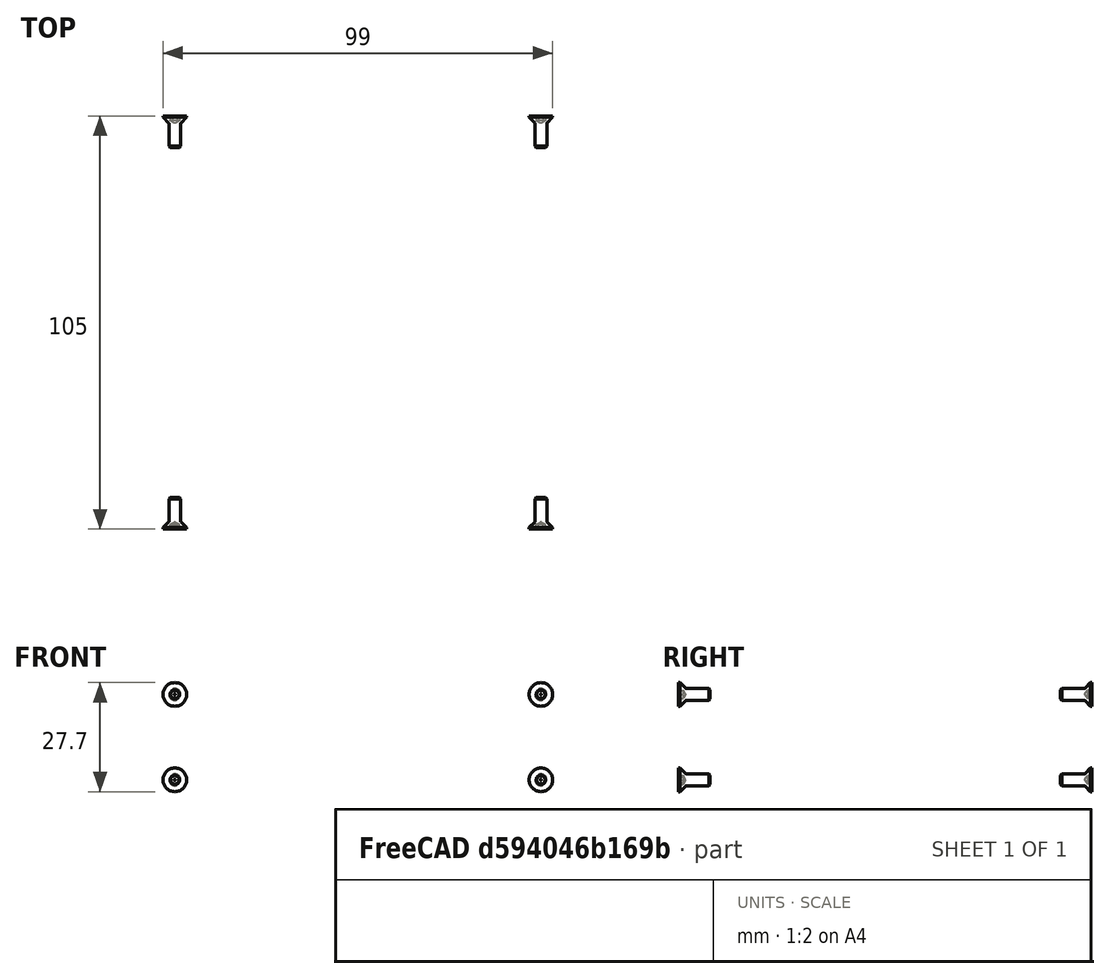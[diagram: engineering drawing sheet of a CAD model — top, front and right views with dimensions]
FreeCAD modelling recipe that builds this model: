
FCSTD DOCUMENT  (FreeCAD 0.19R24267 +99 (Git))
Label: OTP20_Case_Assembly
License: Creative Commons Attribution-NonCommercial-ShareAlike
LicenseURL: http://creativecommons.org/licenses/by-nc-sa/4.0/
objects: Part::FeaturePython×8, App::Link×6, App::DocumentObjectGroup×3, PartDesign::CoordinateSystem×1, App::FeaturePython×1, App::Part×1
note: 9 computed .brp shape members not serialized (recipe doc carries the construction recipe); baked Part::Feature solids carry a one-line shape summary decoded from their .brp
EXTERNAL_REF file=KOH_Plate_Front.FCStd obj=LCS_0
EXTERNAL_REF file=KOH_Plate_Front.FCStd obj=Plate_Front
EXTERNAL_REF file=OTP20_Case_Bezel.FCStd obj=LCS_0
EXTERNAL_REF file=OTP20_Case_Bezel.FCStd obj=Bezel
EXTERNAL_REF file=KOH-2100.FCStd obj=LCS_KOH2100_CornerBottom
EXTERNAL_REF file=KOH_Plate_Front.FCStd obj=LCS_Plate_Front_CornerBottom
EXTERNAL_REF file=KOH-2100.FCStd obj=KOH_2100
EXTERNAL_REF file=KOH-0100.FCStd obj=LCS_0
EXTERNAL_REF file=KOH-0100.FCStd obj=KOH_0100
EXTERNAL_REF file=KOH_Plate_Back.FCStd obj=LCS_Plate_Back_CornerBottom
EXTERNAL_REF file=KOH_Plate_Back.FCStd obj=Plate_Back
EXTERNAL_REF file=KOH_Plate_Back.FCStd obj=LCS_0
EXTERNAL_REF file=KOH_Plate_Front.FCStd obj=LCS_Plate_Front_DisplayCenter
EXTERNAL_REF file=../20_COTS/Waveshare_OLED_0.91in.FCStd obj=LCS_OLEDDisplay_Center
EXTERNAL_REF file=../20_COTS/Waveshare_OLED_0.91in.FCStd obj=OLED_Display

FEATURE [App::DocumentObjectGroup] Parts
FEATURE [PartDesign::CoordinateSystem] LCS_Origin  label="LCS_Case_Origin"
  AttacherType = Attacher::AttachEngine3D
  MapMode = 2
  Support = -> [X_Axis]
FEATURE [App::DocumentObjectGroup] Constraints
FEATURE [App::FeaturePython] Variables  # WARN: FeaturePython — macro-defined, semantics opaque (R4)
FEATURE [App::Link] KOH_Plate_Front_Plate_Front
  AssemblyType = Asm4EE
  AttachedBy = #LCS_0
  AttachedTo = Parent Assembly#LCS_Origin
  LinkedObject = -> <external KOH_Plate_Front.FCStd>#Plate_Front
  expr: Placement = LCS_Origin.Placement * AttachmentOffset * KOH_Plate_Front#LCS_0.Placement ^ -1
FEATURE [App::Link] OTP20_Case_Bezel_Bezel
  AssemblyType = Asm4EE
  AttachedBy = #LCS_0
  AttachedTo = Parent Assembly#LCS_Origin
  AttachmentOffset = pos=(0,2,0) rot=(0,0,1;0rad)
  LinkPlacement = pos=(0,2,0) rot=(0,0,1;0rad)
  LinkedObject = -> <external OTP20_Case_Bezel.FCStd>#Bezel
  Placement = pos=(0,2,0) rot=(0,0,1;0rad)
  expr: Placement = LCS_Origin.Placement * AttachmentOffset * OTP20_Case_Bezel#LCS_0.Placement ^ -1
FEATURE [App::Link] KOH_2100_KOH_2100
  AssemblyType = Asm4EE
  AttachedBy = #LCS_KOH2100_CornerBottom
  AttachedTo = KOH_Plate_Front_Plate_Front#LCS_Plate_Front_CornerBottom
  AttachmentOffset = pos=(0,3,0) rot=(0,0,1;0rad)
  LinkPlacement = pos=(0,3,-14.35) rot=(0,0,1;0rad)
  LinkedObject = -> <external KOH-2100.FCStd>#KOH_2100
  Placement = pos=(0,3,-14.35) rot=(0,0,1;0rad)
  expr: Placement = KOH_Plate_Front_Plate_Front.Placement * KOH_Plate_Front#LCS_Plate_Front_CornerBottom.Placement * AttachmentOffset * KOH_2100#LCS_KOH2100_CornerBottom.Placement ^ -1
FEATURE [App::Link] KOH_0100_KOH_0100
  AssemblyType = Asm4EE
  AttachedBy = #LCS_0
  AttachedTo = KOH_2100_KOH_2100#LCS_KOH2100_CornerBottom
  AttachmentOffset = pos=(105,100,28.7) rot=(0,0,1;3.14159rad)
  LinkPlacement = pos=(52.5,103,14.35) rot=(0,0,1;3.14159rad)
  LinkedObject = -> <external KOH-0100.FCStd>#KOH_0100
  Placement = pos=(52.5,103,14.35) rot=(0,0,1;3.14159rad)
  SolverId = Placement::ExpressionEngine
  expr: Placement = KOH_2100_KOH_2100.Placement * KOH_2100#LCS_KOH2100_CornerBottom.Placement * AttachmentOffset * KOH_0100#LCS_0.Placement ^ -1
FEATURE [App::Link] KOH_Plate_Back_Plate_Back
  AssemblyType = Asm4EE
  AttachedBy = #LCS_Plate_Back_CornerBottom
  AttachedTo = KOH_Plate_Front_Plate_Front#LCS_Plate_Front_CornerBottom
  AttachmentOffset = pos=(0,105,0) rot=(0,0,1;0rad)
  LinkPlacement = pos=(0,105,1.95e-14) rot=(0,0,-1;3.14159rad)
  LinkedObject = -> <external KOH_Plate_Back.FCStd>#Plate_Back
  Placement = pos=(0,105,1.95e-14) rot=(0,0,-1;3.14159rad)
  SolverId = Placement::ExpressionEngine
  expr: Placement = KOH_Plate_Front_Plate_Front.Placement * KOH_Plate_Front#LCS_Plate_Front_CornerBottom.Placement * AttachmentOffset * KOH_Plate_Back#LCS_Plate_Back_CornerBottom.Placement ^ -1
FEATURE [Part::FeaturePython] Screw  label="M3x8-Screw"  # Fasteners workbench fastener (typed FeaturePython)
  AssemblyType = Asm4EE
  AttachedBy = Origin
  AttachedTo = KOH_Plate_Front_Plate_Front#LCS_0
  AttachmentOffset = pos=(46.5,0,10.85) rot=(0,0.707107,-0.707107;3.14159rad)
  Placement = pos=(46.5,0,10.85) rot=(0,0.707107,-0.707107;3.14159rad)
  diameter = 1
  invert = false
  length = 0
  lengthCustom = 8
  matchOuter = false
  offset = 0
  thread = false
  type = 17
  expr: Placement = KOH_Plate_Front_Plate_Front.Placement * KOH_Plate_Front#LCS_0.Placement * AttachmentOffset
FEATURE [Part::FeaturePython] Screw001  label="M3x8-Screw089"  # Fasteners workbench fastener (typed FeaturePython)
  AssemblyType = Asm4EE
  AttachedBy = Origin
  AttachedTo = KOH_Plate_Front_Plate_Front#LCS_0
  AttachmentOffset = pos=(46.5,0,-10.85) rot=(1,0,0;1.5708rad)
  Placement = pos=(46.5,0,-10.85) rot=(1,0,0;1.5708rad)
  diameter = 1
  invert = false
  length = 0
  lengthCustom = 8
  matchOuter = false
  offset = 0
  thread = false
  type = 17
  expr: Placement = KOH_Plate_Front_Plate_Front.Placement * KOH_Plate_Front#LCS_0.Placement * AttachmentOffset
FEATURE [Part::FeaturePython] Screw002  label="M3x8-Screw090"  # Fasteners workbench fastener (typed FeaturePython)
  AssemblyType = Asm4EE
  AttachedBy = Origin
  AttachedTo = KOH_Plate_Front_Plate_Front#LCS_0
  AttachmentOffset = pos=(-46.5,0,10.85) rot=(-1,0,0;4.71239rad)
  Placement = pos=(-46.5,0,10.85) rot=(1,0,0;1.5708rad)
  diameter = 1
  invert = false
  length = 0
  lengthCustom = 8
  matchOuter = false
  offset = 0
  thread = false
  type = 17
  expr: Placement = KOH_Plate_Front_Plate_Front.Placement * KOH_Plate_Front#LCS_0.Placement * AttachmentOffset
FEATURE [Part::FeaturePython] Screw003  label="M3x8-Screw091"  # Fasteners workbench fastener (typed FeaturePython)
  AssemblyType = Asm4EE
  AttachedBy = Origin
  AttachedTo = KOH_Plate_Front_Plate_Front#LCS_0
  AttachmentOffset = pos=(-46.5,0,-10.85) rot=(-0.57735,-0.57735,0.57735;4.18879rad)
  Placement = pos=(-46.5,0,-10.85) rot=(0.57735,0.57735,-0.57735;2.0944rad)
  diameter = 1
  invert = false
  length = 0
  lengthCustom = 8
  matchOuter = false
  offset = 0
  thread = false
  type = 17
  expr: Placement = KOH_Plate_Front_Plate_Front.Placement * KOH_Plate_Front#LCS_0.Placement * AttachmentOffset
FEATURE [Part::FeaturePython] Screw004  label="M3x8-Screw108"  # Fasteners workbench fastener (typed FeaturePython)
  AssemblyType = Asm4EE
  AttachedBy = Origin
  AttachedTo = KOH_Plate_Back_Plate_Back#LCS_0
  AttachmentOffset = pos=(46.5,0,10.85) rot=(-1,0,0;4.71239rad)
  Placement = pos=(-46.5,105,10.85) rot=(0,0.707107,0.707107;3.14159rad)
  diameter = 1
  invert = false
  length = 0
  lengthCustom = 8
  matchOuter = false
  offset = 0
  thread = false
  type = 17
  expr: Placement = KOH_Plate_Back_Plate_Back.Placement * KOH_Plate_Back#LCS_0.Placement * AttachmentOffset
FEATURE [Part::FeaturePython] Screw005  label="M3x8-Screw109"  # Fasteners workbench fastener (typed FeaturePython)
  AssemblyType = Asm4EE
  AttachedBy = Origin
  AttachedTo = KOH_Plate_Back_Plate_Back#LCS_0
  AttachmentOffset = pos=(46.5,0,-10.85) rot=(1,0,0;1.5708rad)
  Placement = pos=(-46.5,105,-10.85) rot=(0,0.707107,0.707107;3.14159rad)
  diameter = 1
  invert = false
  length = 0
  lengthCustom = 8
  matchOuter = false
  offset = 0
  thread = false
  type = 17
  expr: Placement = KOH_Plate_Back_Plate_Back.Placement * KOH_Plate_Back#LCS_0.Placement * AttachmentOffset
FEATURE [Part::FeaturePython] Screw006  label="M3x8-Screw110"  # Fasteners workbench fastener (typed FeaturePython)
  AssemblyType = Asm4EE
  AttachedBy = Origin
  AttachedTo = KOH_Plate_Back_Plate_Back#LCS_0
  AttachmentOffset = pos=(-46.5,0,10.85) rot=(1,0,0;1.5708rad)
  Placement = pos=(46.5,105,10.85) rot=(0,0.707107,0.707107;3.14159rad)
  diameter = 1
  invert = false
  length = 0
  lengthCustom = 8
  matchOuter = false
  offset = 0
  thread = false
  type = 17
  expr: Placement = KOH_Plate_Back_Plate_Back.Placement * KOH_Plate_Back#LCS_0.Placement * AttachmentOffset
FEATURE [Part::FeaturePython] Screw007  label="M3x8-Screw111"  # Fasteners workbench fastener (typed FeaturePython)
  AssemblyType = Asm4EE
  AttachedBy = Origin
  AttachedTo = KOH_Plate_Back_Plate_Back#LCS_0
  AttachmentOffset = pos=(-46.5,0,-10.85) rot=(-1,0,0;4.71239rad)
  Placement = pos=(46.5,105,-10.85) rot=(0,0.707107,0.707107;3.14159rad)
  diameter = 1
  invert = false
  length = 0
  lengthCustom = 8
  matchOuter = false
  offset = 0
  thread = false
  type = 17
  expr: Placement = KOH_Plate_Back_Plate_Back.Placement * KOH_Plate_Back#LCS_0.Placement * AttachmentOffset
FEATURE [App::DocumentObjectGroup] Group  label="Screws"
  Group = -> [Screw,Screw001,Screw002,Screw003,Screw004,Screw005,Screw006,Screw007]
FEATURE [App::Link] Waveshare_OLED_0_91in_OLED_Display
  AssemblyType = Asm4EE
  AttachedBy = #LCS_OLEDDisplay_Center
  AttachedTo = KOH_Plate_Front_Plate_Front#LCS_Plate_Front_DisplayCenter
  AttachmentOffset = pos=(0,-0.09,-2) rot=(0,0,1;3.14159rad)
  LinkPlacement = pos=(36.19,5.3,9.55) rot=(0,-1,0;3.14159rad)
  LinkedObject = -> <external ../20_COTS/Waveshare_OLED_0.91in.FCStd>#OLED_Display
  Placement = pos=(36.19,5.3,9.55) rot=(0,-1,0;3.14159rad)
  expr: Placement = KOH_Plate_Front_Plate_Front.Placement * KOH_Plate_Front#LCS_Plate_Front_DisplayCenter.Placement * AttachmentOffset * Waveshare_OLED_0_91in#LCS_OLEDDisplay_Center.Placement ^ -1
FEATURE [App::Part] Model
  Configuration = 0
  Group = -> [LCS_Origin,Constraints,Variables,KOH_Plate_Front_Plate_Front,OTP20_Case_Bezel_Bezel,KOH_2100_KOH_2100,KOH_0100_KOH_0100,KOH_Plate_Back_Plate_Back,Group,Screw,Screw001,Screw002,Screw003,Screw004,Screw005,Screw006,Screw007,Waveshare_OLED_0_91in_OLED_Display]
  Origin = -> Origin
  Type = Assembly4 Model

RESOLVED EXTERNAL PARTS (link-assembly join: the EXTERNAL_REF files above that resolve inside this repo's crawl, each included once):
---- part ../20_COTS/Waveshare_OLED_0.91in.FCStd = doc fcstd_ae2fe7aa054e ----
FCSTD DOCUMENT  (FreeCAD 0.19R24267 +99 (Git))
Label: Waveshare_OLED_0.91in
License: Creative Commons Attribution-NonCommercial-ShareAlike
LicenseURL: http://creativecommons.org/licenses/by-nc-sa/4.0/
objects: Sketcher::SketchObject×14, PartDesign::Pad×9, PartDesign::Plane×9, PartDesign::Body×7, PartDesign::Pocket×4, PartDesign::Chamfer×4, PartDesign::Mirrored×3, PartDesign::CoordinateSystem×2, PartDesign::Boolean×1, PartDesign::Hole×1, PartDesign::LinearPattern×1, PartDesign::Fillet×1, App::Part×1
note: 75 computed .brp shape members not serialized (recipe doc carries the construction recipe); baked Part::Feature solids carry a one-line shape summary decoded from their .brp

FEATURE [Sketcher::SketchObject] Sketch
  FullyConstrained = true
  MapMode = 5
  Placement = pos=(0,0,0) rot=(1,0,0;1.5708rad)
  Support = -> [XZ_Plane]
  sketch-geometry (4):
    g0: LineSegment StartX=0 StartY=12.5 StartZ=0 EndX=36 EndY=12.5 EndZ=0
    g1: LineSegment StartX=36 StartY=12.5 StartZ=0 EndX=36 EndY=0 EndZ=0
    g2: LineSegment StartX=36 StartY=0 StartZ=0 EndX=0 EndY=0 EndZ=0
    g3: LineSegment StartX=0 StartY=0 StartZ=0 EndX=0 EndY=12.5 EndZ=0
  constraints (11):
    c: Coincident(g0,g1)
    c: Coincident(g1,g2)
    c: Coincident(g2,g3)
    c: Coincident(g3,g0)
    c: Horizontal(g0)
    c: Horizontal(g2)
    c: Vertical(g1)
    c: Vertical(g3)
    c: Distance(g3) = 12.5
    c: Distance(g0) = 36
    c: Coincident(g2,g-1)
FEATURE [PartDesign::Pad] Pad  label="Board Outline"
  Direction = (1,1,1)
  Length = 1.7
  Length2 = 100
  Placement = pos=(0,0,0) rot=(1,0,0;1.5708rad)
  Profile = -> Sketch
  Refine = true
  Type = 0
FEATURE [Sketcher::SketchObject] Sketch001
  FullyConstrained = true
  MapMode = 5
  Placement = pos=(0,0,0) rot=(1,0,0;1.5708rad)
  Support = -> [XZ_Plane]
  sketch-geometry (4):
    g0: LineSegment StartX=4 StartY=11.7 StartZ=0 EndX=34 EndY=11.7 EndZ=0
    g1: LineSegment StartX=34 StartY=11.7 StartZ=0 EndX=34 EndY=0.2 EndZ=0
    g2: LineSegment StartX=34 StartY=0.2 StartZ=0 EndX=4 EndY=0.2 EndZ=0
    g3: LineSegment StartX=4 StartY=0.2 StartZ=0 EndX=4 EndY=11.7 EndZ=0
  constraints (12):
    c: Coincident(g0,g1)
    c: Coincident(g1,g2)
    c: Coincident(g2,g3)
    c: Coincident(g3,g0)
    c: Horizontal(g0)
    c: Horizontal(g2)
    c: Vertical(g1)
    c: Vertical(g3)
    c: Distance(g0) = 30
    c: Distance(g3) = 11.5
    c: Distance(g-1,g3) = 4
    c: Distance(g-1,g2) = 0.2
FEATURE [Sketcher::SketchObject] Sketch003
  FullyConstrained = true
  MapMode = 5
  Placement = pos=(0,0,0) rot=(1,0,0;1.5708rad)
  Support = -> [XZ_Plane]
  sketch-geometry (1):
    g0: Circle CenterX=1 CenterY=2.44 CenterZ=0 NormalX=0 NormalY=0 NormalZ=1 AngleXU=0 Radius=0.5
  constraints (3):
    c: DistanceX(g-2,g0) = 1
    c: Radius(g0) = 0.5
    c: DistanceY(g-1,g0) = 2.44
FEATURE [Sketcher::SketchObject] Sketch004
  FullyConstrained = true
  MapMode = 5
  Placement = pos=(0,0,0) rot=(1,0,0;1.5708rad)
  Support = -> [XZ_Plane001]
  expr: Constraints[20] = Sketch.Constraints[9]
  expr: Constraints[19] = Sketch.Constraints[8]
  sketch-geometry (8):
    g0: LineSegment StartX=29.75 StartY=0.25 StartZ=0 EndX=35.75 EndY=0.25 EndZ=0
    g1: LineSegment StartX=35.75 StartY=0.25 StartZ=0 EndX=35.75 EndY=12.25 EndZ=0
    g2: LineSegment StartX=35.75 StartY=12.25 StartZ=0 EndX=29.75 EndY=12.25 EndZ=0
    g3: LineSegment StartX=29.75 StartY=12.25 StartZ=0 EndX=29.75 EndY=0.25 EndZ=0
    g4: LineSegment StartX=0 StartY=12.5 StartZ=0 EndX=36 EndY=12.5 EndZ=0
    g5: LineSegment StartX=36 StartY=12.5 StartZ=0 EndX=36 EndY=0 EndZ=0
    g6: LineSegment StartX=36 StartY=0 StartZ=0 EndX=0 EndY=0 EndZ=0
    g7: LineSegment StartX=0 StartY=0 StartZ=0 EndX=0 EndY=12.5 EndZ=0
  constraints (23):
    c: Coincident(g0,g1)
    c: Coincident(g1,g2)
    c: Coincident(g2,g3)
    c: Coincident(g3,g0)
    c: Horizontal(g0)
    c: Horizontal(g2)
    c: Vertical(g1)
    c: Vertical(g3)
    c: DistanceY(g0) = 0.25
    c: Distance(g1) = 12
    c: Distance(g2) = 6
    c: Coincident(g4,g5)
    c: Coincident(g5,g6)
    c: Coincident(g6,g7)
    c: Coincident(g7,g4)
    c: Horizontal(g4)
    c: Horizontal(g6)
    c: Vertical(g5)
    c: Vertical(g7)
    c: Distance(g7) = 12.5
    c: Distance(g4) = 36
    c: Coincident(g6,g-1)
    c: Distance(g0,g5) = 0.25
FEATURE [PartDesign::Pad] Pad003
  Direction = (1,1,1)
  Length = 5.5
  Length2 = 100
  Placement = pos=(0,0,0) rot=(1,0,0;1.5708rad)
  Profile = -> Sketch004
  Refine = true
  Reversed = true
  Type = 0
FEATURE [Sketcher::SketchObject] Sketch005
  FullyConstrained = true
  MapMode = 5
  Placement = pos=(35.75,0,0) rot=(0.707107,0,0.707107;3.14159rad)
  Support = -> [Pad003]
  sketch-geometry (9):
    g0: LineSegment StartX=1.85 StartY=-0.8 StartZ=0 EndX=10.65 EndY=-0.8 EndZ=0
    g1: LineSegment StartX=10.65 StartY=-0.8 StartZ=0 EndX=10.65 EndY=-4.6 EndZ=0
    g2: LineSegment StartX=10.65 StartY=-4.6 StartZ=0 EndX=8.25 EndY=-4.6 EndZ=0
    g3: LineSegment StartX=1.85 StartY=-4.6 StartZ=0 EndX=1.85 EndY=-0.8 EndZ=0
    g4: GeomPoint X=6.25 Y=-2.7 Z=0
    g5: LineSegment StartX=4.25 StartY=-4.6 StartZ=0 EndX=4.25 EndY=-5.2 EndZ=0
    g6: LineSegment StartX=4.25 StartY=-5.2 StartZ=0 EndX=8.25 EndY=-5.2 EndZ=0
    g7: LineSegment StartX=8.25 StartY=-5.2 StartZ=0 EndX=8.25 EndY=-4.6 EndZ=0
    g8: LineSegment StartX=4.25 StartY=-4.6 StartZ=0 EndX=1.85 EndY=-4.6 EndZ=0
  constraints (24):
    c: Coincident(g0,g1)
    c: Coincident(g1,g2)
    c: Coincident(g8,g3)
    c: Coincident(g3,g0)
    c: Horizontal(g0)
    c: Horizontal(g2)
    c: Vertical(g1)
    c: Vertical(g3)
    c: Symmetric(g0,g1,g4)
    c: DistanceX(g4) = 6.25
    c: Distance(g1) = 3.8
    c: Distance(g-1,g0) = 0.8
    c: Coincident(g5,g6)
    c: Horizontal(g6)
    c: Coincident(g6,g7)
    c: Vertical(g5)
    c: Coincident(g2,g7)
    c: Coincident(g8,g5)
    c: Tangent(g2,g8)
    c: Vertical(g7)
    c: Distance(g0) = 8.8
    c: Distance(g6) = 4
    c: Distance(g5) = 0.6
    c: Distance(g2) = 2.4
FEATURE [PartDesign::Pocket] Pocket
  BaseFeature = -> Pad003
  Length = 4.5
  Length2 = 100
  Placement = pos=(0,0,0) rot=(1,0,0;1.5708rad)
  Profile = -> Sketch005
  Refine = true
  Type = 0
FEATURE [Sketcher::SketchObject] Sketch006
  FullyConstrained = true
  MapMode = 5
  Placement = pos=(0,8.1e-15,12.25) rot=(0,0,1;3.14159rad)
  Support = -> [Pocket]
  sketch-geometry (8):
    g0: LineSegment StartX=-34.95 StartY=-6 StartZ=0 EndX=-34.95 EndY=-4.6 EndZ=0
    g1: LineSegment StartX=-34.95 StartY=-4.6 StartZ=0 EndX=-33.25 EndY=-4.6 EndZ=0
    g2: LineSegment StartX=-33.25 StartY=-4.6 StartZ=0 EndX=-33.25 EndY=-3.6 EndZ=0
    g3: LineSegment StartX=-33.25 StartY=-3.6 StartZ=0 EndX=-30.75 EndY=-3.6 EndZ=0
    g4: LineSegment StartX=-30.75 StartY=-3.6 StartZ=0 EndX=-30.75 EndY=-2.8 EndZ=0
    g5: LineSegment StartX=-30.75 StartY=-2.8 StartZ=0 EndX=-35.75 EndY=-2.8 EndZ=0
    g6: LineSegment StartX=-35.75 StartY=-2.8 StartZ=0 EndX=-35.75 EndY=-6 EndZ=0
    g7: LineSegment StartX=-35.75 StartY=-6 StartZ=0 EndX=-34.95 EndY=-6 EndZ=0
  constraints (24):
    c: Vertical(g0)
    c: Coincident(g0,g1)
    c: Horizontal(g1)
    c: Coincident(g1,g2)
    c: Vertical(g2)
    c: Coincident(g2,g3)
    c: Horizontal(g3)
    c: Coincident(g3,g4)
    c: Vertical(g4)
    c: Coincident(g4,g5)
    c: Horizontal(g5)
    c: Coincident(g5,g6)
    c: Vertical(g6)
    c: Coincident(g6,g7)
    c: Coincident(g7,g0)
    c: Horizontal(g7)
    c: Distance(g4) = 0.8
    c: Distance(g2) = 1
    c: DistanceY(g0) = -6
    c: DistanceX(g6) = -35.75
    c: Distance(g7) = 0.8
    c: Distance(g1,g6) = 2.5
    c: Distance(g5) = 5
    c: DistanceY(g5) = -2.8
FEATURE [PartDesign::Pocket] Pocket001
  BaseFeature = -> Pocket
  Length = 0.8
  Length2 = 100
  Placement = pos=(0,0,0) rot=(1,0,0;1.5708rad)
  Profile = -> Sketch006
  Refine = true
  Type = 0
FEATURE [PartDesign::Plane] DatumPlane  label="Symmetry Plane"
  AttachmentOffset = pos=(0,0,6.25) rot=(0,0,1;0rad)
  Length = 60
  MapMode = 5
  Placement = pos=(0,0,6.25) rot=(0,0,1;0rad)
  ResizeMode = 0
  Support = -> [XY_Plane001]
  Width = 60
FEATURE [PartDesign::Mirrored] Mirrored
  BaseFeature = -> Pocket001
  MirrorPlane = -> DatumPlane
  Originals = -> [Pocket001]
  Placement = pos=(0,0,0) rot=(1,0,0;1.5708rad)
  Refine = true
FEATURE [Sketcher::SketchObject] Sketch007
  FullyConstrained = true
  MapMode = 5
  Placement = pos=(0,5.5,-2.4e-15) rot=(-1,0,0;1.5708rad)
  Support = -> [Mirrored]
  sketch-geometry (4):
    g0: LineSegment StartX=29.75 StartY=-1.85 StartZ=0 EndX=33.95 EndY=-1.85 EndZ=0
    g1: LineSegment StartX=33.95 StartY=-1.85 StartZ=0 EndX=33.95 EndY=-2.85 EndZ=0
    g2: LineSegment StartX=33.95 StartY=-2.85 StartZ=0 EndX=29.75 EndY=-2.85 EndZ=0
    g3: LineSegment StartX=29.75 StartY=-2.85 StartZ=0 EndX=29.75 EndY=-1.85 EndZ=0
  constraints (12):
    c: Coincident(g0,g1)
    c: Coincident(g1,g2)
    c: Coincident(g2,g3)
    c: Coincident(g3,g0)
    c: Horizontal(g0)
    c: Horizontal(g2)
    c: Vertical(g1)
    c: Vertical(g3)
    c: Distance(g1) = 1
    c: Distance(g0) = 4.2
    c: DistanceX(g2) = 29.75
    c: DistanceY(g0) = -1.85
FEATURE [PartDesign::Pocket] Pocket002
  BaseFeature = -> Mirrored
  Length = 1
  Length2 = 100
  Placement = pos=(0,0,0) rot=(1,0,0;1.5708rad)
  Profile = -> Sketch007
  Refine = true
  Type = 0
FEATURE [PartDesign::Mirrored] Mirrored001
  BaseFeature = -> Pocket002
  MirrorPlane = -> DatumPlane
  Originals = -> [Pocket002]
  Placement = pos=(0,0,0) rot=(1,0,0;1.5708rad)
  Refine = true
FEATURE [Sketcher::SketchObject] Sketch008
  FullyConstrained = true
  MapMode = 5
  Placement = pos=(0,8.1e-15,12.25) rot=(0,0,1;3.14159rad)
  Support = -> [Mirrored001]
  sketch-geometry (4):
    g0: LineSegment StartX=-30 StartY=0 StartZ=0 EndX=-30 EndY=-3.3 EndZ=0
    g1: LineSegment StartX=-30 StartY=-3.3 StartZ=0 EndX=-27.8 EndY=-2.5 EndZ=0
    g2: LineSegment StartX=-27.8 StartY=-2.5 StartZ=0 EndX=-27.8 EndY=0 EndZ=0
    g3: LineSegment StartX=-27.8 StartY=0 StartZ=0 EndX=-30 EndY=0 EndZ=0
  constraints (12):
    c: PointOnObject(g0,g-1)
    c: Vertical(g0)
    c: Coincident(g0,g1)
    c: Coincident(g1,g2)
    c: PointOnObject(g2,g-1)
    c: Vertical(g2)
    c: Coincident(g2,g3)
    c: Coincident(g3,g0)
    c: DistanceX(g0) = -30
    c: Distance(g0) = 3.3
    c: Distance(g3) = 2.2
    c: Distance(g2) = 2.5
FEATURE [PartDesign::Pad] Pad004
  BaseFeature = -> Mirrored001
  Direction = (1,1,1)
  Length = 0.7
  Length2 = 100
  Placement = pos=(0,0,0) rot=(1,0,0;1.5708rad)
  Profile = -> Sketch008
  Refine = true
  Reversed = true
  Type = 0
FEATURE [PartDesign::Mirrored] Mirrored002
  BaseFeature = -> Pad004
  MirrorPlane = -> DatumPlane
  Originals = -> [Pad004]
  Placement = pos=(0,0,0) rot=(1,0,0;1.5708rad)
  Refine = true
FEATURE [PartDesign::Plane] CopyDatumPlane
  Length = 70.8999
  Placement = pos=(0,0,6.25) rot=(0,0,1;0rad)
  ResizeMode = 0
  Width = 60.9499
FEATURE [PartDesign::Plane] DatumPlane001
  AttachmentOffset = pos=(0,0,3) rot=(0,0,1;0rad)
  Length = 60
  MapMode = 5
  Placement = pos=(0,0,9.25) rot=(0,0,1;0rad)
  ResizeMode = 0
  Support = -> [CopyDatumPlane]
  Width = 60
FEATURE [Sketcher::SketchObject] Sketch009
  FullyConstrained = true
  MapMode = 5
  Placement = pos=(0,0,9.25) rot=(0,0,1;0rad)
  Support = -> [DatumPlane001]
  sketch-geometry (12):
    g0: LineSegment StartX=34.95 StartY=2.8 StartZ=0 EndX=29.95 EndY=2.8 EndZ=0
    g1: LineSegment StartX=29.65 StartY=2.5 StartZ=0 EndX=29.65 EndY=0.8 EndZ=0
    g2: LineSegment StartX=28.85 StartY=-1.6e-15 StartZ=0 EndX=27.15 EndY=0 EndZ=0
    g3: LineSegment StartX=27.15 StartY=0 StartZ=0 EndX=27.15 EndY=0.5 EndZ=0
    g4: LineSegment StartX=27.15 StartY=0.5 StartZ=0 EndX=28.85 EndY=0.5 EndZ=0
    g5: LineSegment StartX=29.15 StartY=0.8 StartZ=0 EndX=29.15 EndY=2.5 EndZ=0
    g6: LineSegment StartX=29.95 StartY=3.3 StartZ=0 EndX=34.95 EndY=3.3 EndZ=0
    g7: LineSegment StartX=34.95 StartY=3.3 StartZ=0 EndX=34.95 EndY=2.8 EndZ=0
    g8: ArcOfCircle CenterX=29.95 CenterY=2.5 CenterZ=0 NormalX=0 NormalY=0 NormalZ=1 AngleXU=0 Radius=0.3 StartAngle=1.5708 EndAngle=3.14159
    g9: ArcOfCircle CenterX=28.85 CenterY=0.8 CenterZ=0 NormalX=0 NormalY=0 NormalZ=1 AngleXU=0 Radius=0.8 StartAngle=4.71239 EndAngle=6.28319
    g10: ArcOfCircle CenterX=28.85 CenterY=0.8 CenterZ=0 NormalX=0 NormalY=0 NormalZ=1 AngleXU=0 Radius=0.3 StartAngle=4.71239 EndAngle=6.28319
    g11: ArcOfCircle CenterX=29.95 CenterY=2.5 CenterZ=0 NormalX=0 NormalY=0 NormalZ=1 AngleXU=0 Radius=0.8 StartAngle=1.5708 EndAngle=3.14159
  constraints (30):
    c: Horizontal(g0)
    c: Vertical(g1)
    c: PointOnObject(g2,g-1)
    c: Coincident(g2,g3)
    c: Vertical(g3)
    c: Coincident(g3,g4)
    c: Horizontal(g4)
    c: Vertical(g5)
    c: Horizontal(g6)
    c: Coincident(g6,g7)
    c: Coincident(g7,g0)
    c: Vertical(g7)
    c: Distance(g7) = 0.5
    c: Equal(g3,g7)
    c: DistanceY(g0) = 2.8
    c: DistanceX(g0) = 34.95
    c: Tangent(g1,g8) = -1.5708
    c: Tangent(g0,g8) = -1.5708
    c: Tangent(g2,g9) = 1.5708
    c: Tangent(g1,g9) = 1.5708
    c: Tangent(g4,g10) = -1.5708
    c: Tangent(g5,g10) = -1.5708
    c: Tangent(g5,g11) = 1.5708
    c: Tangent(g6,g11) = 1.5708
    c: Distance(g0,g1) = 5.3
    c: Distance(g1,g3) = 2.5
    c: Coincident(g10,g9)
    c: Coincident(g11,g8)
    c: Radius(g11) = 0.8
    c: Radius(g9) = 0.8
FEATURE [PartDesign::Pad] Pad005
  Direction = (1,1,1)
  Length = 0.5
  Length2 = 100
  Midplane = true
  Placement = pos=(0,0,9.25) rot=(0,0,1;0rad)
  Profile = -> Sketch009
  Refine = true
  Type = 0
FEATURE [PartDesign::Chamfer] Chamfer
  Angle = 45
  Base = -> Pad005 [Edge23,Face2]
  BaseFeature = -> Pad005
  ChamferType = 0
  FlipDirection = false
  Placement = pos=(0,0,9.25) rot=(0,0,1;0rad)
  Refine = true
  Size = 0.2
  Size2 = 1
  SupportTransform = false
FEATURE [PartDesign::Body] Body002  label="Pin001"
  Group = -> [DatumPlane001,CopyDatumPlane,Sketch009,Pad005,Chamfer]
  Origin = -> Origin002
  Tip = -> Chamfer
FEATURE [PartDesign::Plane] CopyDatumPlane001
  Length = 60
  Placement = pos=(0,0,6.25) rot=(0,0,1;0rad)
  ResizeMode = 0
  Width = 60
FEATURE [PartDesign::Plane] DatumPlane002
  AttachmentOffset = pos=(0,0,1) rot=(0,0,1;0rad)
  Length = 60
  MapMode = 5
  Placement = pos=(0,0,7.25) rot=(0,0,1;0rad)
  ResizeMode = 0
  Support = -> [CopyDatumPlane001]
  Width = 60
FEATURE [Sketcher::SketchObject] Sketch010
  FullyConstrained = true
  MapMode = 5
  Placement = pos=(0,0,7.25) rot=(0,0,1;0rad)
  Support = -> [DatumPlane002]
  sketch-geometry (12):
    g0: LineSegment StartX=34.95 StartY=2.8 StartZ=0 EndX=29.95 EndY=2.8 EndZ=0
    g1: LineSegment StartX=29.65 StartY=2.5 StartZ=0 EndX=29.65 EndY=0.8 EndZ=0
    g2: LineSegment StartX=28.85 StartY=-1.6e-15 StartZ=0 EndX=27.15 EndY=0 EndZ=0
    g3: LineSegment StartX=27.15 StartY=0 StartZ=0 EndX=27.15 EndY=0.5 EndZ=0
    g4: LineSegment StartX=27.15 StartY=0.5 StartZ=0 EndX=28.85 EndY=0.5 EndZ=0
    g5: LineSegment StartX=29.15 StartY=0.8 StartZ=0 EndX=29.15 EndY=2.5 EndZ=0
    g6: LineSegment StartX=29.95 StartY=3.3 StartZ=0 EndX=34.95 EndY=3.3 EndZ=0
    g7: LineSegment StartX=34.95 StartY=3.3 StartZ=0 EndX=34.95 EndY=2.8 EndZ=0
    g8: ArcOfCircle CenterX=29.95 CenterY=2.5 CenterZ=0 NormalX=0 NormalY=0 NormalZ=1 AngleXU=0 Radius=0.3 StartAngle=1.5708 EndAngle=3.14159
    g9: ArcOfCircle CenterX=28.85 CenterY=0.8 CenterZ=0 NormalX=0 NormalY=0 NormalZ=1 AngleXU=0 Radius=0.8 StartAngle=4.71239 EndAngle=6.28319
    g10: ArcOfCircle CenterX=28.85 CenterY=0.8 CenterZ=0 NormalX=0 NormalY=0 NormalZ=1 AngleXU=0 Radius=0.3 StartAngle=4.71239 EndAngle=6.28319
    g11: ArcOfCircle CenterX=29.95 CenterY=2.5 CenterZ=0 NormalX=0 NormalY=0 NormalZ=1 AngleXU=0 Radius=0.8 StartAngle=1.5708 EndAngle=3.14159
  constraints (30):
    c: Horizontal(g0)
    c: Vertical(g1)
    c: PointOnObject(g2,g-1)
    c: Coincident(g2,g3)
    c: Vertical(g3)
    c: Coincident(g3,g4)
    c: Horizontal(g4)
    c: Vertical(g5)
    c: Horizontal(g6)
    c: Coincident(g6,g7)
    c: Coincident(g7,g0)
    c: Vertical(g7)
    c: Distance(g7) = 0.5
    c: Equal(g3,g7)
    c: DistanceY(g0) = 2.8
    c: DistanceX(g0) = 34.95
    c: Tangent(g1,g8) = -1.5708
    c: Tangent(g0,g8) = -1.5708
    c: Tangent(g2,g9) = 1.5708
    c: Tangent(g1,g9) = 1.5708
    c: Tangent(g4,g10) = -1.5708
    c: Tangent(g5,g10) = -1.5708
    c: Tangent(g5,g11) = 1.5708
    c: Tangent(g6,g11) = 1.5708
    c: Distance(g0,g1) = 5.3
    c: Distance(g1,g3) = 2.5
    c: Coincident(g10,g9)
    c: Coincident(g11,g8)
    c: Radius(g11) = 0.8
    c: Radius(g9) = 0.8
FEATURE [PartDesign::Pad] Pad006
  Direction = (1,1,1)
  Length = 0.5
  Length2 = 100
  Midplane = true
  Placement = pos=(0,0,7.25) rot=(0,0,1;0rad)
  Profile = -> Sketch010
  Refine = true
  Type = 0
FEATURE [PartDesign::Chamfer] Chamfer001
  Angle = 45
  Base = -> Pad006 [Edge23,Face2]
  BaseFeature = -> Pad006
  ChamferType = 0
  FlipDirection = false
  Placement = pos=(0,0,7.25) rot=(0,0,1;0rad)
  Refine = true
  Size = 0.2
  Size2 = 1
  SupportTransform = false
FEATURE [PartDesign::Body] Body003  label="Pin002"
  Group = -> [DatumPlane002,CopyDatumPlane001,Sketch010,Pad006,Chamfer001]
  Origin = -> Origin003
  Tip = -> Chamfer001
FEATURE [PartDesign::Plane] CopyDatumPlane002
  Length = 60
  Placement = pos=(0,0,6.25) rot=(0,0,1;0rad)
  ResizeMode = 0
  Width = 60
FEATURE [PartDesign::Plane] DatumPlane003
  AttachmentOffset = pos=(0,0,-1) rot=(0,0,1;0rad)
  Length = 60
  MapMode = 5
  Placement = pos=(0,0,5.25) rot=(0,0,1;0rad)
  ResizeMode = 0
  Support = -> [CopyDatumPlane002]
  Width = 60
FEATURE [Sketcher::SketchObject] Sketch011
  FullyConstrained = true
  MapMode = 5
  Placement = pos=(0,0,5.25) rot=(0,0,1;0rad)
  Support = -> [DatumPlane003]
  sketch-geometry (12):
    g0: LineSegment StartX=34.95 StartY=2.8 StartZ=0 EndX=29.95 EndY=2.8 EndZ=0
    g1: LineSegment StartX=29.65 StartY=2.5 StartZ=0 EndX=29.65 EndY=0.8 EndZ=0
    g2: LineSegment StartX=28.85 StartY=-1.6e-15 StartZ=0 EndX=27.15 EndY=0 EndZ=0
    g3: LineSegment StartX=27.15 StartY=0 StartZ=0 EndX=27.15 EndY=0.5 EndZ=0
    g4: LineSegment StartX=27.15 StartY=0.5 StartZ=0 EndX=28.85 EndY=0.5 EndZ=0
    g5: LineSegment StartX=29.15 StartY=0.8 StartZ=0 EndX=29.15 EndY=2.5 EndZ=0
    g6: LineSegment StartX=29.95 StartY=3.3 StartZ=0 EndX=34.95 EndY=3.3 EndZ=0
    g7: LineSegment StartX=34.95 StartY=3.3 StartZ=0 EndX=34.95 EndY=2.8 EndZ=0
    g8: ArcOfCircle CenterX=29.95 CenterY=2.5 CenterZ=0 NormalX=0 NormalY=0 NormalZ=1 AngleXU=0 Radius=0.3 StartAngle=1.5708 EndAngle=3.14159
    g9: ArcOfCircle CenterX=28.85 CenterY=0.8 CenterZ=0 NormalX=0 NormalY=0 NormalZ=1 AngleXU=0 Radius=0.8 StartAngle=4.71239 EndAngle=6.28319
    g10: ArcOfCircle CenterX=28.85 CenterY=0.8 CenterZ=0 NormalX=0 NormalY=0 NormalZ=1 AngleXU=0 Radius=0.3 StartAngle=4.71239 EndAngle=6.28319
    g11: ArcOfCircle CenterX=29.95 CenterY=2.5 CenterZ=0 NormalX=0 NormalY=0 NormalZ=1 AngleXU=0 Radius=0.8 StartAngle=1.5708 EndAngle=3.14159
  constraints (30):
    c: Horizontal(g0)
    c: Vertical(g1)
    c: PointOnObject(g2,g-1)
    c: Coincident(g2,g3)
    c: Vertical(g3)
    c: Coincident(g3,g4)
    c: Horizontal(g4)
    c: Vertical(g5)
    c: Horizontal(g6)
    c: Coincident(g6,g7)
    c: Coincident(g7,g0)
    c: Vertical(g7)
    c: Distance(g7) = 0.5
    c: Equal(g3,g7)
    c: DistanceY(g0) = 2.8
    c: DistanceX(g0) = 34.95
    c: Tangent(g1,g8) = -1.5708
    c: Tangent(g0,g8) = -1.5708
    c: Tangent(g2,g9) = 1.5708
    c: Tangent(g1,g9) = 1.5708
    c: Tangent(g4,g10) = -1.5708
    c: Tangent(g5,g10) = -1.5708
    c: Tangent(g5,g11) = 1.5708
    c: Tangent(g6,g11) = 1.5708
    c: Distance(g0,g1) = 5.3
    c: Distance(g1,g3) = 2.5
    c: Coincident(g10,g9)
    c: Coincident(g11,g8)
    c: Radius(g11) = 0.8
    c: Radius(g9) = 0.8
FEATURE [PartDesign::Pad] Pad007
  Direction = (1,1,1)
  Length = 0.5
  Length2 = 100
  Midplane = true
  Placement = pos=(0,0,5.25) rot=(0,0,1;0rad)
  Profile = -> Sketch011
  Refine = true
  Type = 0
FEATURE [PartDesign::Chamfer] Chamfer002
  Angle = 45
  Base = -> Pad007 [Edge23,Face2]
  BaseFeature = -> Pad007
  ChamferType = 0
  FlipDirection = false
  Placement = pos=(0,0,5.25) rot=(0,0,1;0rad)
  Refine = true
  Size = 0.2
  Size2 = 1
  SupportTransform = false
FEATURE [PartDesign::Body] Body004  label="Pin003"
  Group = -> [DatumPlane003,CopyDatumPlane002,Sketch011,Pad007,Chamfer002]
  Origin = -> Origin004
  Tip = -> Chamfer002
FEATURE [PartDesign::Plane] CopyDatumPlane003
  Length = 60
  Placement = pos=(0,0,6.25) rot=(0,0,1;0rad)
  ResizeMode = 0
  Width = 60
FEATURE [PartDesign::Plane] DatumPlane004
  AttachmentOffset = pos=(0,0,-3) rot=(0,0,1;0rad)
  Length = 60
  MapMode = 5
  Placement = pos=(0,0,3.25) rot=(0,0,1;0rad)
  ResizeMode = 0
  Support = -> [CopyDatumPlane003]
  Width = 60
FEATURE [Sketcher::SketchObject] Sketch012
  FullyConstrained = true
  MapMode = 5
  Placement = pos=(0,0,3.25) rot=(0,0,1;0rad)
  Support = -> [DatumPlane004]
  sketch-geometry (12):
    g0: LineSegment StartX=34.95 StartY=2.8 StartZ=0 EndX=29.95 EndY=2.8 EndZ=0
    g1: LineSegment StartX=29.65 StartY=2.5 StartZ=0 EndX=29.65 EndY=0.8 EndZ=0
    g2: LineSegment StartX=28.85 StartY=-1.6e-15 StartZ=0 EndX=27.15 EndY=0 EndZ=0
    g3: LineSegment StartX=27.15 StartY=0 StartZ=0 EndX=27.15 EndY=0.5 EndZ=0
    g4: LineSegment StartX=27.15 StartY=0.5 StartZ=0 EndX=28.85 EndY=0.5 EndZ=0
    g5: LineSegment StartX=29.15 StartY=0.8 StartZ=0 EndX=29.15 EndY=2.5 EndZ=0
    g6: LineSegment StartX=29.95 StartY=3.3 StartZ=0 EndX=34.95 EndY=3.3 EndZ=0
    g7: LineSegment StartX=34.95 StartY=3.3 StartZ=0 EndX=34.95 EndY=2.8 EndZ=0
    g8: ArcOfCircle CenterX=29.95 CenterY=2.5 CenterZ=0 NormalX=0 NormalY=0 NormalZ=1 AngleXU=0 Radius=0.3 StartAngle=1.5708 EndAngle=3.14159
    g9: ArcOfCircle CenterX=28.85 CenterY=0.8 CenterZ=0 NormalX=0 NormalY=0 NormalZ=1 AngleXU=0 Radius=0.8 StartAngle=4.71239 EndAngle=6.28319
    g10: ArcOfCircle CenterX=28.85 CenterY=0.8 CenterZ=0 NormalX=0 NormalY=0 NormalZ=1 AngleXU=0 Radius=0.3 StartAngle=4.71239 EndAngle=6.28319
    g11: ArcOfCircle CenterX=29.95 CenterY=2.5 CenterZ=0 NormalX=0 NormalY=0 NormalZ=1 AngleXU=0 Radius=0.8 StartAngle=1.5708 EndAngle=3.14159
  constraints (30):
    c: Horizontal(g0)
    c: Vertical(g1)
    c: PointOnObject(g2,g-1)
    c: Coincident(g2,g3)
    c: Vertical(g3)
    c: Coincident(g3,g4)
    c: Horizontal(g4)
    c: Vertical(g5)
    c: Horizontal(g6)
    c: Coincident(g6,g7)
    c: Coincident(g7,g0)
    c: Vertical(g7)
    c: Distance(g7) = 0.5
    c: Equal(g3,g7)
    c: DistanceY(g0) = 2.8
    c: DistanceX(g0) = 34.95
    c: Tangent(g1,g8) = -1.5708
    c: Tangent(g0,g8) = -1.5708
    c: Tangent(g2,g9) = 1.5708
    c: Tangent(g1,g9) = 1.5708
    c: Tangent(g4,g10) = -1.5708
    c: Tangent(g5,g10) = -1.5708
    c: Tangent(g5,g11) = 1.5708
    c: Tangent(g6,g11) = 1.5708
    c: Distance(g0,g1) = 5.3
    c: Distance(g1,g3) = 2.5
    c: Coincident(g10,g9)
    c: Coincident(g11,g8)
    c: Radius(g11) = 0.8
    c: Radius(g9) = 0.8
FEATURE [PartDesign::Pad] Pad008
  Direction = (1,1,1)
  Length = 0.5
  Length2 = 100
  Midplane = true
  Placement = pos=(0,0,3.25) rot=(0,0,1;0rad)
  Profile = -> Sketch012
  Refine = true
  Type = 0
FEATURE [PartDesign::Chamfer] Chamfer003
  Angle = 45
  Base = -> Pad008 [Edge23,Face2]
  BaseFeature = -> Pad008
  ChamferType = 0
  FlipDirection = false
  Placement = pos=(0,0,3.25) rot=(0,0,1;0rad)
  Refine = true
  Size = 0.2
  Size2 = 1
  SupportTransform = false
FEATURE [PartDesign::Body] Body005  label="Pin004"
  Group = -> [DatumPlane004,CopyDatumPlane003,Sketch012,Pad008,Chamfer003]
  Origin = -> Origin005
  Tip = -> Chamfer003
FEATURE [PartDesign::Boolean] Boolean
  BaseFeature = -> Mirrored002
  Group = -> [Body002,Body003,Body004,Body005]
  Refine = true
  Type = 0
FEATURE [PartDesign::Body] Body001  label="Connector PH2.0"
  Group = -> [Sketch004,Pad003,Sketch005,Pocket,Sketch006,Pocket001,DatumPlane,Mirrored,Sketch007,Pocket002,Mirrored001,Sketch008,Pad004,Mirrored002,Boolean]
  Origin = -> Origin001
  Tip = -> Boolean
FEATURE [PartDesign::Pad] Pad001  label="Display Glas"
  BaseFeature = -> Pad
  Direction = (1,1,1)
  Length = 3.3
  Length2 = 100
  Placement = pos=(0,0,0) rot=(1,0,0;1.5708rad)
  Profile = -> Sketch001
  Refine = true
  Type = 0
FEATURE [Sketcher::SketchObject] Sketch002
  FullyConstrained = true
  MapMode = 5
  Placement = pos=(0,-3.3,1.5e-15) rot=(1,0,0;1.5708rad)
  Support = -> [Pad001]
  sketch-geometry (5):
    g0: LineSegment StartX=5.8 StartY=9.98 StartZ=0 EndX=28.18 EndY=9.98 EndZ=0
    g1: LineSegment StartX=28.18 StartY=9.98 StartZ=0 EndX=28.18 EndY=4.4 EndZ=0
    g2: LineSegment StartX=28.18 StartY=4.4 StartZ=0 EndX=5.8 EndY=4.4 EndZ=0
    g3: LineSegment StartX=5.8 StartY=4.4 StartZ=0 EndX=5.8 EndY=9.98 EndZ=0
    g4: GeomPoint X=16.99 Y=7.19 Z=0
  constraints (15):
    c: Coincident(g0,g1)
    c: Coincident(g1,g2)
    c: Coincident(g2,g3)
    c: Coincident(g3,g0)
    c: Horizontal(g0)
    c: Horizontal(g2)
    c: Vertical(g1)
    c: Vertical(g3)
    c: Distance(g0) = 22.38
    c: Distance(g3) = 5.58
    c: Distance(g-1,g3) = 5.8
    c: Distance(g-1,g2) = 4.4
    c: Symmetric(g0,g1,g4)
    c: DistanceX(g4) = 16.99
    c: DistanceY(g4) = 7.19
FEATURE [PartDesign::Pocket] Pocket003  label="Display Active Area"
  BaseFeature = -> Pad001
  Length = 0.1
  Length2 = 100
  Placement = pos=(0,0,0) rot=(1,0,0;1.5708rad)
  Profile = -> Sketch002
  Refine = true
  Type = 0
FEATURE [PartDesign::Hole] Hole
  BaseFeature = -> Pocket003
  Depth = 25
  DepthType = 0
  Diameter = 0.8
  DrillForDepth = false
  DrillPoint = 1
  DrillPointAngle = 118
  HoleCutCountersinkAngle = 90
  HoleCutCustomValues = false
  HoleCutDepth = 0
  HoleCutDiameter = 0
  HoleCutType = 0
  ModelActualThread = false
  Placement = pos=(0,0,0) rot=(1,0,0;1.5708rad)
  Profile = -> Sketch003
  Refine = true
  Reversed = true
  Tapered = false
  TaperedAngle = 90
  ThreadAngle = 0
  ThreadClass = 0
  ThreadCutOffInner = 0
  ThreadCutOffOuter = 0
  ThreadDirection = 0
  ThreadFit = 0
  ThreadPitch = 0
  ThreadSize = 0
  ThreadType = 0
  Threaded = false
FEATURE [PartDesign::LinearPattern] LinearPattern
  BaseFeature = -> Hole
  Direction = -> Z_Axis
  Length = 7.62
  Occurrences = 4
  Originals = -> [Hole]
  Placement = pos=(0,0,0) rot=(1,0,0;1.5708rad)
  Refine = true
FEATURE [PartDesign::Fillet] Fillet
  Base = -> LinearPattern [Edge2,Edge8,Edge1,Edge5]
  BaseFeature = -> LinearPattern
  Placement = pos=(0,0,0) rot=(1,0,0;1.5708rad)
  Radius = 0.5
  Refine = true
  SupportTransform = false
FEATURE [PartDesign::Body] Body  label="Mainboard"
  Group = -> [Sketch,Pad,Sketch001,Pad001,Pocket003,Sketch002,Sketch003,Hole,LinearPattern,Fillet]
  Origin = -> Origin
  Tip = -> Fillet
FEATURE [Sketcher::SketchObject] Sketch013
  FullyConstrained = true
  MapMode = 5
  Placement = pos=(0,0,0) rot=(1,0,0;1.5708rad)
  Support = -> [XZ_Plane006]
  sketch-geometry (6):
    g0: LineSegment StartX=19.5 StartY=1.7 StartZ=0 EndX=19.5 EndY=8.7 EndZ=0
    g1: LineSegment StartX=19.5 StartY=8.7 StartZ=0 EndX=6.5 EndY=8.7 EndZ=0
    g2: LineSegment StartX=6.5 StartY=8.7 StartZ=0 EndX=6.5 EndY=11.7 EndZ=0
    g3: LineSegment StartX=6.5 StartY=11.7 StartZ=0 EndX=21.5 EndY=11.7 EndZ=0
    g4: LineSegment StartX=21.5 StartY=11.7 StartZ=0 EndX=21.5 EndY=1.7 EndZ=0
    g5: LineSegment StartX=21.5 StartY=1.7 StartZ=0 EndX=19.5 EndY=1.7 EndZ=0
  constraints (18):
    c: Vertical(g0)
    c: Coincident(g0,g1)
    c: Horizontal(g1)
    c: Coincident(g1,g2)
    c: Vertical(g2)
    c: Coincident(g2,g3)
    c: Horizontal(g3)
    c: Coincident(g3,g4)
    c: Vertical(g4)
    c: Coincident(g4,g5)
    c: Coincident(g5,g0)
    c: Horizontal(g5)
    c: Distance(g5) = 2
    c: Distance(g2) = 3
    c: DistanceY(g3) = 11.7
    c: Distance(g4) = 10
    c: DistanceX(g3) = 21.5
    c: DistanceX(g2) = 6.5
FEATURE [PartDesign::Pad] Pad009
  Direction = (1,1,1)
  Length = 1.2
  Length2 = 100
  Placement = pos=(0,0,0) rot=(1,0,0;1.5708rad)
  Profile = -> Sketch013
  Refine = true
  Reversed = true
  Type = 0
FEATURE [PartDesign::Body] Body006  label="Components"
  Group = -> [Sketch013,Pad009]
  Origin = -> Origin006
  Tip = -> Pad009
FEATURE [PartDesign::CoordinateSystem] LCS_0
  AttacherType = Attacher::AttachEngine3D
  MapMode = 2
  Support = -> [X_Axis007]
FEATURE [PartDesign::CoordinateSystem] LCS_OLEDDisplay_Center
  AttacherType = Attacher::AttachEngine3D
  AttachmentOffset = pos=(16.99,7.19,3.3) rot=(0,0,1;0rad)
  MapMode = 5
  Placement = pos=(16.99,-3.3,7.19) rot=(1,0,0;1.5708rad)
  Support = -> [XZ_Plane007]
  expr: .AttachmentOffset.Base.x = Sketch002.Constraints[13]
  expr: .AttachmentOffset.Base.y = Sketch002.Constraints[14]
  expr: .AttachmentOffset.Base.z = <<Display Glas>>.Length
FEATURE [App::Part] OLED_Display
  Group = -> [LCS_0,LCS_OLEDDisplay_Center,Body,Body001,Body006]
  Origin = -> Origin007
---- part KOH-0100.FCStd = doc fcstd_208fa9221306 ----
FCSTD DOCUMENT  (FreeCAD 0.19R24267 +99 (Git))
Label: KOH-0100
License: All rights reserved
LicenseURL: http://en.wikipedia.org/wiki/All_rights_reserved
objects: Part::FeaturePython×2, Part::Feature×1, Part::Compound×1, PartDesign::CoordinateSystem×1, PartDesign::Plane×1, App::Part×1
note: 6 computed .brp shape members not serialized (recipe doc carries the construction recipe); baked Part::Feature solids carry a one-line shape summary decoded from their .brp

FEATURE [Part::Feature] Part__Feature  label="KOH 0"
  Placement = pos=(0,0,0) rot=(-1,0,0;1.5708rad)
  shape: bbox 105 x 160 x 8.533 mm, 128 faces (baked)
FEATURE [Part::Compound] Compound
  Links = -> [Part__Feature]
FEATURE [PartDesign::CoordinateSystem] LCS_0  label="LCS_KOH0100_CornerTop"
  AttacherType = Attacher::AttachEngine3D
  MapMode = 2
  Support = -> [X_Axis]
FEATURE [PartDesign::Plane] Offset
  AttachmentOffset = pos=(0,0,100) rot=(0,0,1;0rad)
  Length = 100
  MapMode = 5
  Placement = pos=(0,100,2.22e-14) rot=(0,0.707107,0.707107;3.14159rad)
  ResizeMode = 1
  Support = -> [XZ_Plane]
  Width = 100
FEATURE [Part::FeaturePython] Slice  # WARN: FeaturePython — macro-defined, semantics opaque (R4)
  Base = -> Compound
  Mode = 1
  Tolerance = 0
  Tools = -> [Offset]
FEATURE [Part::FeaturePython] Slice_child0  label="Slice.0"  # WARN: FeaturePython — macro-defined, semantics opaque (R4)
  Base = -> Slice
  FilterType = 1
  Invert = false
  OverrideMaxVal = 0
  WindowFrom = 80
  WindowTo = 100
  items = 0
FEATURE [App::Part] KOH_0100
  Group = -> [LCS_0,Part__Feature,Compound,Offset,Slice,Slice_child0]
  Origin = -> Origin
---- part KOH_Plate_Back.FCStd = doc fcstd_df4504fd72fb ----
FCSTD DOCUMENT  (FreeCAD 0.19R24267 +99 (Git))
Label: KOH_Plate_Back
License: All rights reserved
LicenseURL: http://en.wikipedia.org/wiki/All_rights_reserved
objects: Sketcher::SketchObject×2, PartDesign::CoordinateSystem×2, PartDesign::Pad×1, PartDesign::Fillet×1, PartDesign::Hole×1, PartDesign::Body×1, App::Part×1
note: 11 computed .brp shape members not serialized (recipe doc carries the construction recipe); baked Part::Feature solids carry a one-line shape summary decoded from their .brp

FEATURE [Sketcher::SketchObject] Sketch
  FullyConstrained = true
  MapMode = 5
  Placement = pos=(0,0,0) rot=(1,0,0;1.5708rad)
  Support = -> [XZ_Plane]
  sketch-geometry (4):
    g0: LineSegment StartX=-52.5 StartY=-14.35 StartZ=0 EndX=52.5 EndY=-14.35 EndZ=0
    g1: LineSegment StartX=52.5 StartY=-14.35 StartZ=0 EndX=52.5 EndY=14.35 EndZ=0
    g2: LineSegment StartX=52.5 StartY=14.35 StartZ=0 EndX=-52.5 EndY=14.35 EndZ=0
    g3: LineSegment StartX=-52.5 StartY=14.35 StartZ=0 EndX=-52.5 EndY=-14.35 EndZ=0
  constraints (10):
    c: Coincident(g0,g1)
    c: Coincident(g1,g2)
    c: Coincident(g2,g3)
    c: Coincident(g3,g0)
    c: Horizontal(g0)
    c: Vertical(g1)
    c: Symmetric(g2,g0,g-1)
    c: Symmetric(g2,g1,g-2)
    c: Distance(g2) = 105
    c: Distance(g3) = 28.7
FEATURE [PartDesign::Pad] Pad
  Direction = (1,1,1)
  Length = 2
  Length2 = 100
  Placement = pos=(0,0,0) rot=(1,0,0;1.5708rad)
  Profile = -> Sketch
  Refine = true
  Reversed = true
  Type = 0
FEATURE [PartDesign::Fillet] Fillet
  Base = -> Pad [Edge5,Edge2,Edge8,Edge1]
  BaseFeature = -> Pad
  Placement = pos=(0,0,0) rot=(1,0,0;1.5708rad)
  Radius = 2.5
  Refine = true
  SupportTransform = false
FEATURE [Sketcher::SketchObject] Sketch001
  FullyConstrained = true
  MapMode = 5
  Placement = pos=(0,0,0) rot=(1,0,0;1.5708rad)
  Support = -> [XZ_Plane]
  expr: Constraints[9] = Sketch.Constraints[9]
  expr: Constraints[8] = Sketch.Constraints[8]
  sketch-geometry (8):
    g0: LineSegment StartX=-52.5 StartY=-14.35 StartZ=0 EndX=52.5 EndY=-14.35 EndZ=0
    g1: LineSegment StartX=52.5 StartY=-14.35 StartZ=0 EndX=52.5 EndY=14.35 EndZ=0
    g2: LineSegment StartX=52.5 StartY=14.35 StartZ=0 EndX=-52.5 EndY=14.35 EndZ=0
    g3: LineSegment StartX=-52.5 StartY=14.35 StartZ=0 EndX=-52.5 EndY=-14.35 EndZ=0
    g4: Circle CenterX=46.5 CenterY=10.85 CenterZ=0 NormalX=0 NormalY=0 NormalZ=1 AngleXU=0 Radius=1.6
    g5: Circle CenterX=46.5 CenterY=-10.85 CenterZ=0 NormalX=0 NormalY=0 NormalZ=1 AngleXU=0 Radius=1.6
    g6: Circle CenterX=-46.5 CenterY=-10.85 CenterZ=0 NormalX=0 NormalY=0 NormalZ=1 AngleXU=0 Radius=1.6
    g7: Circle CenterX=-46.5 CenterY=10.85 CenterZ=0 NormalX=0 NormalY=0 NormalZ=1 AngleXU=0 Radius=1.6
  constraints (19):
    c: Coincident(g0,g1)
    c: Coincident(g1,g2)
    c: Coincident(g2,g3)
    c: Coincident(g3,g0)
    c: Horizontal(g0)
    c: Vertical(g1)
    c: Symmetric(g2,g0,g-1)
    c: Symmetric(g2,g1,g-2)
    c: Distance(g2) = 105
    c: Distance(g3) = 28.7
    c: Distance(g4,g2) = 3.5
    c: DistanceX(g-2,g4) = 46.5
    c: Diameter(g4) = 3.2
    c: Diameter(g5) = 3.2
    c: Symmetric(g5,g4,g-1)
    c: Diameter(g7) = 3.2
    c: Diameter(g6) = 3.2
    c: Symmetric(g7,g6,g-1)
    c: Symmetric(g7,g4,g-2)
FEATURE [PartDesign::Hole] Hole
  BaseFeature = -> Fillet
  Depth = 25
  DepthType = 0
  Diameter = 3.2
  DrillForDepth = false
  DrillPoint = 1
  DrillPointAngle = 118
  HoleCutCountersinkAngle = 90
  HoleCutCustomValues = false
  HoleCutDepth = 0
  HoleCutDiameter = 6.8
  HoleCutType = 2
  ModelActualThread = false
  Placement = pos=(0,0,0) rot=(1,0,0;1.5708rad)
  Profile = -> Sketch001
  Refine = true
  Tapered = false
  TaperedAngle = 90
  ThreadAngle = 0
  ThreadClass = 0
  ThreadCutOffInner = 0
  ThreadCutOffOuter = 0
  ThreadDirection = 0
  ThreadFit = 0
  ThreadPitch = 0
  ThreadSize = 0
  ThreadType = 0
  Threaded = false
FEATURE [PartDesign::Body] Body
  Group = -> [Sketch,Pad,Fillet,Sketch001,Hole]
  Origin = -> Origin
  Tip = -> Hole
FEATURE [PartDesign::CoordinateSystem] LCS_0  label="LCS_PlateBack_Center"
  AttacherType = Attacher::AttachEngine3D
  MapMode = 2
  Support = -> [X_Axis001]
FEATURE [PartDesign::CoordinateSystem] LCS_Plate_Back_CornerBottom
  AttacherType = Attacher::AttachEngine3D
  AttachmentOffset = pos=(52.5,-14.35,0) rot=(0,0.707107,0.707107;3.14159rad)
  MapMode = 5
  Placement = pos=(52.5,3.2e-15,-14.35) rot=(0,0,1;3.14159rad)
  Support = -> [XZ_Plane001]
FEATURE [App::Part] Plate_Back
  Group = -> [LCS_0,Body,LCS_Plate_Back_CornerBottom]
  Origin = -> Origin001
---- part KOH_Plate_Front.FCStd = doc fcstd_8556a17b28e3 ----
FCSTD DOCUMENT  (FreeCAD 0.19R24267 +99 (Git))
Label: KOH_Plate_Front
License: All rights reserved
LicenseURL: http://en.wikipedia.org/wiki/All_rights_reserved
objects: Sketcher::SketchObject×6, PartDesign::Hole×4, PartDesign::CoordinateSystem×3, PartDesign::Fillet×2, PartDesign::Pad×1, PartDesign::Pocket×1, PartDesign::Chamfer×1, PartDesign::Body×1, App::Part×1
note: 28 computed .brp shape members not serialized (recipe doc carries the construction recipe); baked Part::Feature solids carry a one-line shape summary decoded from their .brp

FEATURE [Sketcher::SketchObject] Sketch
  FullyConstrained = true
  MapMode = 5
  Placement = pos=(0,0,0) rot=(1,0,0;1.5708rad)
  Support = -> [XZ_Plane]
  sketch-geometry (4):
    g0: LineSegment StartX=-52.5 StartY=-14.35 StartZ=0 EndX=52.5 EndY=-14.35 EndZ=0
    g1: LineSegment StartX=52.5 StartY=-14.35 StartZ=0 EndX=52.5 EndY=14.35 EndZ=0
    g2: LineSegment StartX=52.5 StartY=14.35 StartZ=0 EndX=-52.5 EndY=14.35 EndZ=0
    g3: LineSegment StartX=-52.5 StartY=14.35 StartZ=0 EndX=-52.5 EndY=-14.35 EndZ=0
  constraints (10):
    c: Coincident(g0,g1)
    c: Coincident(g1,g2)
    c: Coincident(g2,g3)
    c: Coincident(g3,g0)
    c: Horizontal(g0)
    c: Vertical(g1)
    c: Symmetric(g2,g0,g-1)
    c: Symmetric(g2,g1,g-2)
    c: Distance(g2) = 105
    c: Distance(g3) = 28.7
FEATURE [PartDesign::Pad] Pad
  Direction = (1,1,1)
  Length = 2
  Length2 = 100
  Placement = pos=(0,0,0) rot=(1,0,0;1.5708rad)
  Profile = -> Sketch
  Refine = true
  Reversed = true
  Type = 0
FEATURE [PartDesign::Fillet] Fillet
  Base = -> Pad [Edge5,Edge2,Edge8,Edge1]
  BaseFeature = -> Pad
  Placement = pos=(0,0,0) rot=(1,0,0;1.5708rad)
  Radius = 2.5
  Refine = true
  SupportTransform = false
FEATURE [Sketcher::SketchObject] Sketch001
  FullyConstrained = true
  MapMode = 5
  Placement = pos=(0,0,0) rot=(1,0,0;1.5708rad)
  Support = -> [XZ_Plane]
  expr: Constraints[9] = Sketch.Constraints[9]
  expr: Constraints[8] = Sketch.Constraints[8]
  sketch-geometry (8):
    g0: LineSegment StartX=-52.5 StartY=-14.35 StartZ=0 EndX=52.5 EndY=-14.35 EndZ=0
    g1: LineSegment StartX=52.5 StartY=-14.35 StartZ=0 EndX=52.5 EndY=14.35 EndZ=0
    g2: LineSegment StartX=52.5 StartY=14.35 StartZ=0 EndX=-52.5 EndY=14.35 EndZ=0
    g3: LineSegment StartX=-52.5 StartY=14.35 StartZ=0 EndX=-52.5 EndY=-14.35 EndZ=0
    g4: Circle CenterX=46.5 CenterY=10.85 CenterZ=0 NormalX=0 NormalY=0 NormalZ=1 AngleXU=0 Radius=1.6
    g5: Circle CenterX=46.5 CenterY=-10.85 CenterZ=0 NormalX=0 NormalY=0 NormalZ=1 AngleXU=0 Radius=1.6
    g6: Circle CenterX=-46.5 CenterY=-10.85 CenterZ=0 NormalX=0 NormalY=0 NormalZ=1 AngleXU=0 Radius=1.6
    g7: Circle CenterX=-46.5 CenterY=10.85 CenterZ=0 NormalX=0 NormalY=0 NormalZ=1 AngleXU=0 Radius=1.6
  constraints (20):
    c: Coincident(g0,g1)
    c: Coincident(g1,g2)
    c: Coincident(g2,g3)
    c: Coincident(g3,g0)
    c: Horizontal(g0)
    c: Vertical(g1)
    c: Symmetric(g2,g0,g-1)
    c: Symmetric(g2,g1,g-2)
    c: Distance(g2) = 105
    c: Distance(g3) = 28.7
    c: Distance(g4,g2) = 3.5
    c: DistanceX(g-2,g4) = 46.5
    c: Diameter(g4) = 3.2
    c: Diameter(g5) = 3.2
    c: Symmetric(g5,g4,g-1)
    c: Diameter(g7) = 3.2
    c: Diameter(g6) = 3.2
    c: Symmetric(g7,g6,g-1)
    c: Symmetric(g7,g4,g-2)
    c: Distance(g4,g5) = 21.7
FEATURE [PartDesign::Hole] Hole
  BaseFeature = -> Fillet
  Depth = 25
  DepthType = 0
  Diameter = 3.2
  DrillForDepth = false
  DrillPoint = 1
  DrillPointAngle = 118
  HoleCutCountersinkAngle = 90
  HoleCutCustomValues = false
  HoleCutDepth = 0
  HoleCutDiameter = 6.8
  HoleCutType = 2
  ModelActualThread = false
  Placement = pos=(0,0,0) rot=(1,0,0;1.5708rad)
  Profile = -> Sketch001
  Refine = true
  Tapered = false
  TaperedAngle = 90
  ThreadAngle = 0
  ThreadClass = 0
  ThreadCutOffInner = 0
  ThreadCutOffOuter = 0
  ThreadDirection = 0
  ThreadFit = 0
  ThreadPitch = 0
  ThreadSize = 0
  ThreadType = 0
  Threaded = false
FEATURE [Sketcher::SketchObject] Sketch002  label="Cutout_FrontPanel"
  FullyConstrained = true
  MapMode = 5
  Placement = pos=(0,0,0) rot=(1,0,0;1.5708rad)
  Support = -> [XZ_Plane]
  expr: Constraints[37] = Constraints[36]
  sketch-geometry (20):
    g0: LineSegment StartX=-47.4 StartY=1.44 StartZ=0 EndX=-38.6 EndY=1.44 EndZ=0
    g1: LineSegment StartX=-38.6 StartY=1.44 StartZ=0 EndX=-38.6 EndY=-1.56 EndZ=0
    g2: LineSegment StartX=-38.6 StartY=-1.56 StartZ=0 EndX=-47.4 EndY=-1.56 EndZ=0
    g3: LineSegment StartX=-47.4 StartY=-1.56 StartZ=0 EndX=-47.4 EndY=1.44 EndZ=0
    g4: LineSegment StartX=-33 StartY=5.45 StartZ=0 EndX=-19 EndY=5.45 EndZ=0
    g5: LineSegment StartX=-19 StartY=5.45 StartZ=0 EndX=-19 EndY=-0.55 EndZ=0
    g6: LineSegment StartX=-19 StartY=-0.55 StartZ=0 EndX=-33 EndY=-0.55 EndZ=0
    g7: LineSegment StartX=-33 StartY=-0.55 StartZ=0 EndX=-33 EndY=5.45 EndZ=0
    g8: LineSegment StartX=-15 StartY=5.45 StartZ=0 EndX=-1 EndY=5.45 EndZ=0
    g9: LineSegment StartX=-1 StartY=5.45 StartZ=0 EndX=-1 EndY=-0.55 EndZ=0
    g10: LineSegment StartX=-1 StartY=-0.55 StartZ=0 EndX=-15 EndY=-0.55 EndZ=0
    g11: LineSegment StartX=-15 StartY=-0.55 StartZ=0 EndX=-15 EndY=5.45 EndZ=0
    g12: LineSegment StartX=7.45 StartY=5.7 StartZ=0 EndX=30.95 EndY=5.7 EndZ=0
    g13: LineSegment StartX=30.95 StartY=5.7 StartZ=0 EndX=30.95 EndY=-0.8 EndZ=0
    g14: LineSegment StartX=30.95 StartY=-0.8 StartZ=0 EndX=7.45 EndY=-0.8 EndZ=0
    g15: LineSegment StartX=7.45 StartY=-0.8 StartZ=0 EndX=7.45 EndY=5.7 EndZ=0
    g16: GeomPoint X=-8 Y=2.45 Z=0
    g17: GeomPoint X=-26 Y=2.45 Z=0
    g18: GeomPoint X=-43 Y=-0.06 Z=0
    g19: GeomPoint X=19.2 Y=2.45 Z=0
  constraints (55):
    c: Coincident(g0,g1)
    c: Coincident(g1,g2)
    c: Coincident(g2,g3)
    c: Coincident(g3,g0)
    c: Horizontal(g0)
    c: Horizontal(g2)
    c: Vertical(g1)
    c: Vertical(g3)
    c: Coincident(g4,g5)
    c: Coincident(g5,g6)
    c: Coincident(g6,g7)
    c: Coincident(g7,g4)
    c: Horizontal(g4)
    c: Horizontal(g6)
    c: Vertical(g5)
    c: Vertical(g7)
    c: Coincident(g8,g9)
    c: Coincident(g9,g10)
    c: Coincident(g10,g11)
    c: Coincident(g11,g8)
    c: Horizontal(g8)
    c: Horizontal(g10)
    c: Vertical(g9)
    c: Vertical(g11)
    c: Coincident(g12,g13)
    c: Coincident(g13,g14)
    c: Coincident(g14,g15)
    c: Coincident(g15,g12)
    c: Horizontal(g12)
    c: Horizontal(g14)
    c: Vertical(g13)
    c: Vertical(g15)
    c: Horizontal(g4,g8)
    c: Horizontal(g5,g10)
    c: Distance(g-1,g3) = 47.4
    c: Distance(g2) = 8.8
    c: Distance(g6) = 14
    c: Distance(g10) = 14
    c: Distance(g3) = 3
    c: Distance(g-1,g2) = 1.56
    c: Distance(g-1,g6) = 0.55
    c: Distance(g7) = 6
    c: Distance(g12) = 23.5
    c: Distance(g13) = 6.5
    c: Distance(g6,g1) = 5.6
    c: Symmetric(g8,g9,g16)
    c: Symmetric(g5,g4,g17)
    c: DistanceX(g17,g16) = 18
    c: Symmetric(g0,g1,g18)
    c: DistanceX(g18,g17) = 17
    c: Symmetric(g12,g13,g19)
    c: Horizontal(g16,g19)
    c: DistanceX(g19) = 19.2  'DisplayCenter_X'
    c: DistanceX(g8) = -15
    c: DistanceY(g19) = 2.45  'DisplayCenter_Z'
FEATURE [PartDesign::Pocket] Pocket
  BaseFeature = -> Hole
  Length = 5
  Length2 = 100
  Placement = pos=(0,0,0) rot=(1,0,0;1.5708rad)
  Profile = -> Sketch002
  Refine = true
  Type = 1
FEATURE [PartDesign::Fillet] Fillet001
  Base = -> Pocket [Edge69,Edge73,Edge83,Edge68,Edge76,Edge72,Edge82,Edge77,Edge75,Edge67,Edge71,Edge81,Edge84,Edge74,Edge70,Edge78]
  BaseFeature = -> Pocket
  Placement = pos=(0,0,0) rot=(1,0,0;1.5708rad)
  Radius = 0.75
  Refine = true
  SupportTransform = false
FEATURE [PartDesign::Chamfer] Chamfer
  Angle = 45
  Base = -> Fillet001 [Edge40,Edge24,Edge4,Edge32]
  BaseFeature = -> Fillet001
  ChamferType = 0
  FlipDirection = false
  Placement = pos=(0,0,0) rot=(1,0,0;1.5708rad)
  Refine = true
  Size = 0.5
  Size2 = 1
  SupportTransform = false
FEATURE [Sketcher::SketchObject] Sketch003
  FullyConstrained = true
  MapMode = 5
  Placement = pos=(0,0,0) rot=(1,0,0;1.5708rad)
  Support = -> [XZ_Plane]
  sketch-geometry (3):
    g0: Circle CenterX=38 CenterY=0.94 CenterZ=0 NormalX=0 NormalY=0 NormalZ=1 AngleXU=0 Radius=0.5
    g1: Circle CenterX=38 CenterY=3.48 CenterZ=0 NormalX=0 NormalY=0 NormalZ=1 AngleXU=0 Radius=0.5
    g2: LineSegment StartX=38 StartY=0.94 StartZ=0 EndX=38 EndY=3.48 EndZ=0
  constraints (8):
    c: Diameter(g0) = 1
    c: DistanceX(g-2,g0) = 38
    c: Diameter(g1) = 1
    c: Coincident(g0,g2)
    c: Coincident(g1,g2)
    c: Distance(g2) = 2.54
    c: Angle(g2) = 1.5708
    c: DistanceY(g-1,g0) = 0.94
FEATURE [PartDesign::Hole] Hole001
  BaseFeature = -> Chamfer
  Depth = 25
  DepthType = 0
  Diameter = 1.95
  DrillForDepth = false
  DrillPoint = 1
  DrillPointAngle = 118
  HoleCutCountersinkAngle = 90
  HoleCutCustomValues = false
  HoleCutDepth = 0
  HoleCutDiameter = 6.1
  HoleCutType = 0
  ModelActualThread = false
  Placement = pos=(0,0,0) rot=(1,0,0;1.5708rad)
  Profile = -> Sketch003
  Refine = true
  Tapered = false
  TaperedAngle = 90
  ThreadAngle = 0
  ThreadClass = 0
  ThreadCutOffInner = 0
  ThreadCutOffOuter = 0
  ThreadDirection = 0
  ThreadFit = 0
  ThreadPitch = 0
  ThreadSize = 0
  ThreadType = 0
  Threaded = false
FEATURE [Sketcher::SketchObject] Sketch004
  FullyConstrained = true
  MapMode = 5
  Placement = pos=(0,0,0) rot=(1,0,0;1.5708rad)
  Support = -> [XZ_Plane]
  sketch-geometry (1):
    g0: Circle CenterX=46.5 CenterY=0 CenterZ=0 NormalX=0 NormalY=0 NormalZ=1 AngleXU=0 Radius=2.5
  constraints (3):
    c: PointOnObject(g0,g-1)
    c: DistanceX(g-2,g0) = 46.5
    c: Diameter(g0) = 5
FEATURE [PartDesign::CoordinateSystem] LCS_0  label="LCS_PlateFront_Center"
  AttacherType = Attacher::AttachEngine3D
  MapMode = 2
  Support = -> [X_Axis001]
FEATURE [PartDesign::Hole] Hole002
  BaseFeature = -> Hole001
  Depth = 25
  DepthType = 0
  Diameter = 6
  DrillForDepth = false
  DrillPoint = 1
  DrillPointAngle = 118
  HoleCutCountersinkAngle = 90
  HoleCutCustomValues = false
  HoleCutDepth = 0
  HoleCutDiameter = 6.1
  HoleCutType = 0
  ModelActualThread = false
  Placement = pos=(0,0,0) rot=(1,0,0;1.5708rad)
  Profile = -> Sketch004
  Refine = true
  Tapered = false
  TaperedAngle = 90
  ThreadAngle = 0
  ThreadClass = 0
  ThreadCutOffInner = 0
  ThreadCutOffOuter = 0
  ThreadDirection = 0
  ThreadFit = 0
  ThreadPitch = 0
  ThreadSize = 0
  ThreadType = 0
  Threaded = false
FEATURE [Sketcher::SketchObject] Sketch005
  FullyConstrained = false
  MapMode = 5
  Placement = pos=(0,0,0) rot=(1,0,0;1.5708rad)
  Support = -> [XZ_Plane]
  sketch-geometry (8):
    g0: LineSegment StartX=4.18177 StartY=10.0524 StartZ=0 EndX=34.1388 EndY=10.0524 EndZ=0
    g1: LineSegment StartX=34.1388 StartY=10.0524 StartZ=0 EndX=34.1388 EndY=-3.89591 EndZ=0
    g2: LineSegment StartX=34.1388 StartY=-3.89591 StartZ=0 EndX=4.18177 EndY=-3.89591 EndZ=0
    g3: LineSegment StartX=4.18177 StartY=-3.89591 StartZ=0 EndX=4.18177 EndY=10.0524 EndZ=0
    g4: Circle CenterX=4.18177 CenterY=10.0524 CenterZ=0 NormalX=0 NormalY=0 NormalZ=1 AngleXU=0 Radius=1.30359
    g5: Circle CenterX=34.1388 CenterY=10.0524 CenterZ=0 NormalX=0 NormalY=0 NormalZ=1 AngleXU=0 Radius=1.36838
    g6: Circle CenterX=34.1388 CenterY=-3.89591 CenterZ=0 NormalX=0 NormalY=0 NormalZ=1 AngleXU=0 Radius=1.83105
    g7: Circle CenterX=4.18177 CenterY=-3.89591 CenterZ=0 NormalX=0 NormalY=0 NormalZ=1 AngleXU=0 Radius=1.53393
  constraints (12):
    c: Coincident(g0,g1)
    c: Coincident(g1,g2)
    c: Coincident(g2,g3)
    c: Coincident(g3,g0)
    c: Horizontal(g0)
    c: Horizontal(g2)
    c: Vertical(g1)
    c: Vertical(g3)
    c: Coincident(g4,g0)
    c: Coincident(g5,g0)
    c: Coincident(g6,g1)
    c: Coincident(g7,g2)
FEATURE [PartDesign::Hole] Hole003
  BaseFeature = -> Hole002
  Depth = 25
  DepthType = 0
  Diameter = 1.6
  DrillForDepth = false
  DrillPoint = 1
  DrillPointAngle = 118
  HoleCutCountersinkAngle = 90
  HoleCutCustomValues = false
  HoleCutDepth = 0
  HoleCutDiameter = 3
  HoleCutType = 2
  ModelActualThread = false
  Placement = pos=(0,0,0) rot=(1,0,0;1.5708rad)
  Profile = -> Sketch005
  Refine = true
  Tapered = false
  TaperedAngle = 90
  ThreadAngle = 0
  ThreadClass = 0
  ThreadCutOffInner = 0
  ThreadCutOffOuter = 0
  ThreadDirection = 0
  ThreadFit = 0
  ThreadPitch = 0
  ThreadSize = 0
  ThreadType = 0
  Threaded = false
FEATURE [PartDesign::Body] Body
  Group = -> [Sketch,Pad,Fillet,Sketch001,Hole,Sketch002,Pocket,Fillet001,Chamfer,Sketch003,Hole001,Sketch004,Hole002,Sketch005,Hole003]
  Origin = -> Origin
  Tip = -> Hole002
FEATURE [PartDesign::CoordinateSystem] LCS_Plate_Front_CornerBottom
  AttacherType = Attacher::AttachEngine3D
  AttachmentOffset = pos=(-52.5,-14.35,0) rot=(-1,0,0;1.5708rad)
  MapMode = 5
  Placement = pos=(-52.5,3.2e-15,-14.35) rot=(0,0,1;0rad)
  Support = -> [XZ_Plane001]
FEATURE [PartDesign::CoordinateSystem] LCS_Plate_Front_DisplayCenter
  AttacherType = Attacher::AttachEngine3D
  AttachmentOffset = pos=(19.2,2.45,0) rot=(0,0,1;0rad)
  MapMode = 5
  Placement = pos=(19.2,-5e-16,2.45) rot=(1,0,0;1.5708rad)
  Support = -> [XZ_Plane001]
  expr: .AttachmentOffset.Base.x = Sketch002.Constraints.DisplayCenter_X
  expr: .AttachmentOffset.Base.y = Sketch002.Constraints.DisplayCenter_Z
FEATURE [App::Part] Plate_Front
  Group = -> [LCS_0,Body,LCS_Plate_Front_CornerBottom,LCS_Plate_Front_DisplayCenter]
  Origin = -> Origin001
---- part OTP20_Case_Bezel.FCStd = doc fcstd_8eea7158c41d ----
FCSTD DOCUMENT  (FreeCAD 0.19R24267 +99 (Git))
Label: OTP20_Case_Bezel
License: All rights reserved
LicenseURL: http://en.wikipedia.org/wiki/All_rights_reserved
objects: Sketcher::SketchObject×15, PartDesign::Pad×13, PartDesign::Body×5, PartDesign::Fillet×5, PartDesign::Plane×4, PartDesign::LinearPattern×4, PartDesign::Mirrored×3, PartDesign::MultiTransform×3, PartDesign::Thickness×2, PartDesign::Pocket×2, PartDesign::Hole×2, PartDesign::CoordinateSystem×1, PartDesign::Boolean×1, PartDesign::Chamfer×1, App::Part×1
note: 86 computed .brp shape members not serialized (recipe doc carries the construction recipe); baked Part::Feature solids carry a one-line shape summary decoded from their .brp

FEATURE [PartDesign::Plane] DatumPlane
  AttachmentOffset = pos=(0,0,2.5) rot=(0,0,1;0rad)
  Length = 60
  MapMode = 2
  Placement = pos=(0,-2.5,-6e-16) rot=(1,0,0;1.5708rad)
  ResizeMode = 0
  Support = -> [XZ_Plane001]
  Width = 60
  expr: .AttachmentOffset.Base.z = Pad002.Length
FEATURE [Sketcher::SketchObject] Sketch  label="Sketch001"
  FullyConstrained = true
  MapMode = 5
  Placement = pos=(0,-2.5,-6e-16) rot=(1,0,0;1.5708rad)
  Support = -> [DatumPlane]
  sketch-geometry (6):
    g0: LineSegment StartX=55 StartY=6.95 StartZ=0 EndX=55 EndY=10.45 EndZ=0
    g1: LineSegment StartX=55 StartY=10.45 StartZ=0 EndX=54.2 EndY=10.45 EndZ=0
    g2: ArcOfCircle CenterX=54.2 CenterY=10.25 CenterZ=0 NormalX=0 NormalY=0 NormalZ=1 AngleXU=0 Radius=0.2 StartAngle=1.5708 EndAngle=3.14159
    g3: LineSegment StartX=54 StartY=10.25 StartZ=0 EndX=54 EndY=7.15 EndZ=0
    g4: ArcOfCircle CenterX=54.2 CenterY=7.15 CenterZ=0 NormalX=0 NormalY=0 NormalZ=1 AngleXU=0 Radius=0.2 StartAngle=3.14159 EndAngle=4.71239
    g5: LineSegment StartX=54.2 StartY=6.95 StartZ=0 EndX=55 EndY=6.95 EndZ=0
  constraints (16):
    c: Vertical(g0)
    c: Coincident(g0,g1)
    c: Horizontal(g1)
    c: Tangent(g1,g2) = -1.5708
    c: Tangent(g3,g4) = -1.5708
    c: Coincident(g5,g0)
    c: Vertical(g3)
    c: Tangent(g4,g5) = -1.5708
    c: Tangent(g2,g3) = -1.5708
    c: Horizontal(g5)
    c: Vertical(g2,g4)
    c: Radius(g4) = 0.2
    c: Distance(g0,g3) = 1
    c: Distance(g0) = 3.5
    c: Distance(g-1,g5) = 6.95
    c: Distance(g-1,g3) = 54
FEATURE [PartDesign::LinearPattern] LinearPattern
  Direction = -> Sketch [V_Axis]
  Length = 17.4
  Occurrences = 4
  Refine = true
  Reversed = true
FEATURE [PartDesign::Mirrored] Mirrored
  MirrorPlane = -> Sketch [V_Axis]
  Refine = true
FEATURE [Sketcher::SketchObject] Sketch001  label="Sketch002"
  FullyConstrained = true
  MapMode = 5
  Placement = pos=(0,-2.5,-6e-16) rot=(1,0,0;1.5708rad)
  Support = -> [DatumPlane]
  sketch-geometry (6):
    g0: LineSegment StartX=44.65 StartY=16.85 StartZ=0 EndX=44.65 EndY=16.05 EndZ=0
    g1: ArcOfCircle CenterX=44.85 CenterY=16.05 CenterZ=0 NormalX=0 NormalY=0 NormalZ=1 AngleXU=0 Radius=0.2 StartAngle=3.14159 EndAngle=4.71239
    g2: LineSegment StartX=44.85 StartY=15.85 StartZ=0 EndX=47.95 EndY=15.85 EndZ=0
    g3: ArcOfCircle CenterX=47.95 CenterY=16.05 CenterZ=0 NormalX=0 NormalY=0 NormalZ=1 AngleXU=0 Radius=0.2 StartAngle=4.71239 EndAngle=6.28319
    g4: LineSegment StartX=48.15 StartY=16.05 StartZ=0 EndX=48.15 EndY=16.85 EndZ=0
    g5: LineSegment StartX=48.15 StartY=16.85 StartZ=0 EndX=44.65 EndY=16.85 EndZ=0
  constraints (16):
    c: Vertical(g0)
    c: Tangent(g0,g1) = -1.5708
    c: Tangent(g1,g2) = -1.5708
    c: Tangent(g2,g3) = -1.5708
    c: Tangent(g3,g4) = -1.5708
    c: Coincident(g4,g5)
    c: Coincident(g5,g0)
    c: Horizontal(g5)
    c: Horizontal(g2)
    c: Vertical(g4)
    c: Horizontal(g1,g3)
    c: Radius(g3) = 0.2
    c: Distance(g0,g2) = 1
    c: Distance(g5) = 3.5
    c: Distance(g-1,g2) = 15.85
    c: Distance(g-1,g0) = 44.65
FEATURE [PartDesign::LinearPattern] LinearPattern001
  Direction = -> Sketch001 [H_Axis]
  Length = 92.8
  Occurrences = 17
  Refine = true
  Reversed = true
FEATURE [PartDesign::Mirrored] Mirrored001
  MirrorPlane = -> Sketch001 [H_Axis]
  Refine = true
FEATURE [PartDesign::CoordinateSystem] LCS_0  label="LCS_Bezel_Center"
  AttacherType = Attacher::AttachEngine3D
  MapMode = 2
  Support = -> [X_Axis002]
FEATURE [Sketcher::SketchObject] Sketch004  label="Sketch005"
  FullyConstrained = true
  MapMode = 5
  Placement = pos=(0,0,0) rot=(1,0,0;1.5708rad)
  Support = -> [XZ_Plane003]
  sketch-geometry (1):
    g0: Circle CenterX=46.5 CenterY=0 CenterZ=0 NormalX=0 NormalY=0 NormalZ=1 AngleXU=0 Radius=2.9
  constraints (3):
    c: PointOnObject(g0,g-1)
    c: Radius(g0) = 2.9
    c: DistanceX(g0) = 46.5
FEATURE [Sketcher::SketchObject] Sketch005  label="Sketch006"
  FullyConstrained = true
  MapMode = 5
  Placement = pos=(0,0,0) rot=(1,0,0;1.5708rad)
  Support = -> [XZ_Plane003]
  sketch-geometry (5):
    g0: LineSegment StartX=41.5 StartY=1 StartZ=0 EndX=50.5 EndY=1 EndZ=0
    g1: LineSegment StartX=50.5 StartY=1 StartZ=0 EndX=50.5 EndY=-1 EndZ=0
    g2: LineSegment StartX=50.5 StartY=-1 StartZ=0 EndX=41.5 EndY=-1 EndZ=0
    g3: LineSegment StartX=41.5 StartY=-1 StartZ=0 EndX=41.5 EndY=1 EndZ=0
    g4: GeomPoint X=46 Y=0 Z=0
  constraints (13):
    c: Coincident(g0,g1)
    c: Coincident(g1,g2)
    c: Coincident(g2,g3)
    c: Coincident(g3,g0)
    c: Horizontal(g0)
    c: Horizontal(g2)
    c: Vertical(g1)
    c: Vertical(g3)
    c: PointOnObject(g4,g-1)
    c: Symmetric(g0,g1,g4)
    c: Distance(g1) = 2
    c: DistanceX(g0) = 50.5
    c: Distance(g2) = 9
FEATURE [PartDesign::Pad] Pad004
  Direction = (1,1,1)
  Length = 1
  Length2 = 100
  Placement = pos=(0,0,0) rot=(1,0,0;1.5708rad)
  Profile = -> Sketch005
  Refine = true
  Reversed = true
  Type = 0
FEATURE [PartDesign::Pad] Pad005
  BaseFeature = -> Pad004
  Direction = (1,1,1)
  Length = 1
  Length2 = 100
  Placement = pos=(0,0,0) rot=(1,0,0;1.5708rad)
  Profile = -> Sketch004
  Refine = true
  Reversed = true
  Type = 0
FEATURE [PartDesign::Plane] DatumPlane001  label="Display Start"
  AttachmentOffset = pos=(0,0,0.2) rot=(0,0,1;0rad)
  Length = 60
  MapMode = 5
  Placement = pos=(0.2,0,0) rot=(0.57735,0.57735,0.57735;2.0944rad)
  ResizeMode = 0
  Support = -> [YZ_Plane004]
  Width = 60
FEATURE [Sketcher::SketchObject] Sketch006  label="Sketch007"
  FullyConstrained = true
  MapMode = 5
  Placement = pos=(0.2,0,0) rot=(0.57735,0.57735,0.57735;2.0944rad)
  Support = -> [DatumPlane001]
  sketch-geometry (7):
    g0: LineSegment StartX=1 StartY=14.35 StartZ=0 EndX=1 EndY=10.35 EndZ=0
    g1: ArcOfCircle CenterX=4.1 CenterY=9.55 CenterZ=0 NormalX=0 NormalY=0 NormalZ=1 AngleXU=0 Radius=0.8 StartAngle=3.14159 EndAngle=6.28319
    g2: LineSegment StartX=3.3 StartY=9.55 StartZ=0 EndX=0 EndY=9.55 EndZ=0
    g3: LineSegment StartX=0 StartY=9.55 StartZ=0 EndX=0 EndY=14.35 EndZ=0
    g4: LineSegment StartX=0 StartY=14.35 StartZ=0 EndX=1 EndY=14.35 EndZ=0
    g5: LineSegment StartX=1 StartY=10.35 StartZ=0 EndX=4.9 EndY=10.35 EndZ=0
    g6: LineSegment StartX=4.9 StartY=10.35 StartZ=0 EndX=4.9 EndY=9.55 EndZ=0
  constraints (22):
    c: Vertical(g0)
    c: Coincident(g2,g3)
    c: Coincident(g3,g4)
    c: Coincident(g4,g0)
    c: Distance(g4) = 1
    c: Horizontal(g4)
    c: Radius(g1) = 0.8
    c: DistanceY(g0) = 14.35
    c: Horizontal(g1,g1)
    c: Horizontal(g1,g1)
    c: Vertical(g3)
    c: Horizontal(g2)
    c: Coincident(g0,g5)
    c: Horizontal(g5)
    c: Coincident(g5,g6)
    c: Coincident(g6,g1)
    c: Vertical(g6)
    c: Distance(g6) = 0.8
    c: Coincident(g2,g1)
    c: DistanceX(g1) = 3.3
    c: PointOnObject(g2,g-2)
    c: DistanceY(g1) = 9.55
FEATURE [Sketcher::SketchObject] Sketch007  label="Sketch008"
  FullyConstrained = true
  MapMode = 5
  Placement = pos=(0.2,0,0) rot=(0.57735,0.57735,0.57735;2.0944rad)
  Support = -> [DatumPlane001]
  sketch-geometry (7):
    g0: LineSegment StartX=1 StartY=-14.35 StartZ=0 EndX=1 EndY=-4.56714 EndZ=0
    g1: LineSegment StartX=1 StartY=-4.56714 StartZ=0 EndX=4.5 EndY=-3.95 EndZ=0
    g2: LineSegment StartX=4.5 StartY=-3.95 StartZ=0 EndX=4.5 EndY=-2.95 EndZ=0
    g3: ArcOfCircle CenterX=3.9 CenterY=-2.95 CenterZ=0 NormalX=0 NormalY=0 NormalZ=1 AngleXU=0 Radius=0.6 StartAngle=0 EndAngle=3.14159
    g4: LineSegment StartX=3.3 StartY=-2.95 StartZ=0 EndX=0 EndY=-3.53188 EndZ=0
    g5: LineSegment StartX=0 StartY=-3.53188 StartZ=0 EndX=0 EndY=-14.35 EndZ=0
    g6: LineSegment StartX=0 StartY=-14.35 StartZ=0 EndX=1 EndY=-14.35 EndZ=0
  constraints (21):
    c: Vertical(g0)
    c: Coincident(g0,g1)
    c: Coincident(g1,g2)
    c: Tangent(g2,g3) = -1.5708
    c: Coincident(g3,g4)
    c: PointOnObject(g4,g-2)
    c: Coincident(g4,g5)
    c: PointOnObject(g5,g-2)
    c: Coincident(g5,g6)
    c: Coincident(g6,g0)
    c: Horizontal(g6)
    c: Distance(g6) = 1
    c: Radius(g3) = 0.6
    c: Vertical(g2)
    c: Distance(g2) = 1
    c: DistanceX(g3) = 3.3
    c: DistanceY(g3) = -2.95
    c: DistanceY(g5) = -14.35
    c: Horizontal(g3,g3)
    c: Parallel(g4,g1)
    c: Angle(g-1,g4) = 0.174533
FEATURE [Sketcher::SketchObject] Sketch008  label="Sketch009"
  FullyConstrained = true
  MapMode = 5
  Placement = pos=(0.2,0,0) rot=(0.57735,0.57735,0.57735;2.0944rad)
  Support = -> [DatumPlane001]
  expr: Constraints[19] = Sketch006.Constraints[19] + Sketch006.Constraints[6]
  expr: Constraints[14] = Sketch006.Constraints[17]
  expr: Constraints[5] = Sketch006.Constraints[6]
  expr: Constraints[6] = Sketch006.Constraints[7]
  expr: Constraints[3] = Sketch006.Constraints[4]
  expr: Constraints[20] = Sketch006.Constraints[21]
  sketch-geometry (7):
    g0: LineSegment StartX=1 StartY=14.35 StartZ=0 EndX=1 EndY=10.35 EndZ=0
    g1: ArcOfCircle CenterX=4.1 CenterY=9.55 CenterZ=0 NormalX=0 NormalY=0 NormalZ=1 AngleXU=0 Radius=0.8 StartAngle=4.71239 EndAngle=6.28319
    g2: LineSegment StartX=0 StartY=8.75 StartZ=0 EndX=0 EndY=14.35 EndZ=0
    g3: LineSegment StartX=0 StartY=14.35 StartZ=0 EndX=1 EndY=14.35 EndZ=0
    g4: LineSegment StartX=1 StartY=10.35 StartZ=0 EndX=4.9 EndY=10.35 EndZ=0
    g5: LineSegment StartX=4.9 StartY=10.35 StartZ=0 EndX=4.9 EndY=9.55 EndZ=0
    g6: LineSegment StartX=0 StartY=8.75 StartZ=0 EndX=4.1 EndY=8.75 EndZ=0
  constraints (21):
    c: Vertical(g0)
    c: Coincident(g2,g3)
    c: Coincident(g3,g0)
    c: Distance(g3) = 1
    c: Horizontal(g3)
    c: Radius(g1) = 0.8
    c: DistanceY(g0) = 14.35
    c: Horizontal(g1,g1)
    c: Vertical(g2)
    c: Coincident(g0,g4)
    c: Horizontal(g4)
    c: Coincident(g4,g5)
    c: Coincident(g5,g1)
    c: Vertical(g5)
    c: Distance(g5) = 0.8
    c: PointOnObject(g2,g-2)
    c: Coincident(g6,g2)
    c: Horizontal(g6)
    c: Tangent(g1,g6) = -1.5708
    c: DistanceX(g1) = 4.1
    c: DistanceY(g1) = 9.55
FEATURE [PartDesign::Plane] DatumPlane002  label="Display End"
  AttachmentOffset = pos=(0,0,36) rot=(0,0,1;0rad)
  Length = 60
  MapMode = 5
  Placement = pos=(36.2,-4e-15,4e-15) rot=(0.57735,0.57735,0.57735;2.0944rad)
  ResizeMode = 0
  Support = -> [DatumPlane001]
  Width = 60
FEATURE [PartDesign::Pad] Pad006
  Direction = (1,1,1)
  Length = 36
  Length2 = 36
  Placement = pos=(0.2,0,0) rot=(0.57735,0.57735,0.57735;2.0944rad)
  Profile = -> Sketch006
  Refine = true
  Type = 3
  UpToFace = -> DatumPlane002 [Plane]
FEATURE [PartDesign::Pad] Pad007
  Direction = (1,1,1)
  Length = 36
  Length2 = 100
  Placement = pos=(0.2,0,0) rot=(0.57735,0.57735,0.57735;2.0944rad)
  Profile = -> Sketch007
  Refine = true
  Type = 3
  UpToFace = -> DatumPlane002 [Plane]
FEATURE [PartDesign::Pad] Pad008
  BaseFeature = -> Pad006
  Direction = (1,1,1)
  Length = 1
  Length2 = 100
  Placement = pos=(0.2,0,0) rot=(0.57735,0.57735,0.57735;2.0944rad)
  Profile = -> Sketch008
  Refine = true
  Reversed = true
  Type = 0
FEATURE [PartDesign::Plane] DatumPlane003  label="Display Symmetry"
  AttachmentOffset = pos=(0,0,18) rot=(0,0,1;0rad)
  Length = 60
  MapMode = 5
  Placement = pos=(18.2,-2e-15,2e-15) rot=(0.57735,0.57735,0.57735;2.0944rad)
  ResizeMode = 0
  Support = -> [DatumPlane001]
  Width = 60
  expr: .AttachmentOffset.Base.z = <<Display End>>.AttachmentOffset.Base[2] * 0.5
FEATURE [PartDesign::Mirrored] Mirrored002
  BaseFeature = -> Pad008
  MirrorPlane = -> DatumPlane003
  Originals = -> [Pad008]
  Placement = pos=(0.2,0,0) rot=(0.57735,0.57735,0.57735;2.0944rad)
  Refine = true
FEATURE [PartDesign::Body] Body003  label="Display Frame Top"
  Group = -> [Sketch006,Pad006,Sketch008,Pad008,DatumPlane001,DatumPlane002,DatumPlane003,Mirrored002]
  Origin = -> Origin004
  Tip = -> Mirrored002
FEATURE [Sketcher::SketchObject] Sketch009  label="Sketch010"
  FullyConstrained = true
  MapMode = 5
  Placement = pos=(0.2,0,0) rot=(0.57735,0.57735,0.57735;2.0944rad)
  Support = -> [DatumPlane001]
  expr: Constraints[4] = Sketch007.Constraints[14]
  expr: Constraints[2] = Sketch007.Constraints[12]
  expr: Constraints[5] = Sketch007.Constraints[11]
  expr: Constraints[6] = Sketch007.Constraints[20]
  expr: Constraints[11] = Sketch007.Constraints[15] + Sketch007.Constraints[12]
  expr: Constraints[13] = Sketch007.Constraints[16]
  expr: Constraints[19] = Sketch007.Constraints[17]
  sketch-geometry (7):
    g0: LineSegment StartX=1 StartY=-4.56714 StartZ=0 EndX=4.5 EndY=-3.95 EndZ=0
    g1: LineSegment StartX=4.5 StartY=-3.95 StartZ=0 EndX=4.5 EndY=-2.95 EndZ=0
    g2: ArcOfCircle CenterX=3.9 CenterY=-2.95 CenterZ=0 NormalX=0 NormalY=0 NormalZ=1 AngleXU=0 Radius=0.6 StartAngle=0 EndAngle=1.5708
    g3: LineSegment StartX=3.9 StartY=-2.35 StartZ=0 EndX=0 EndY=-2.35 EndZ=0
    g4: LineSegment StartX=0 StartY=-2.35 StartZ=0 EndX=0 EndY=-14.35 EndZ=0
    g5: LineSegment StartX=0 StartY=-14.35 StartZ=0 EndX=1 EndY=-14.35 EndZ=0
    g6: LineSegment StartX=1 StartY=-14.35 StartZ=0 EndX=1 EndY=-4.56714 EndZ=0
  constraints (20):
    c: Coincident(g0,g1)
    c: Tangent(g1,g2) = -1.5708
    c: Radius(g2) = 0.6
    c: Vertical(g1)
    c: Distance(g1) = 1
    c: DistanceX(g0) = 1
    c: Angle(g-1,g0) = 0.174533
    c: PointOnObject(g3,g-2)
    c: Horizontal(g3)
    c: Coincident(g3,g4)
    c: PointOnObject(g4,g-2)
    c: DistanceX(g2) = 3.9
    c: Tangent(g2,g3) = -1.5708
    c: DistanceY(g2) = -2.95
    c: Coincident(g4,g5)
    c: Horizontal(g5)
    c: Coincident(g5,g6)
    c: Coincident(g6,g0)
    c: Vertical(g6)
    c: DistanceY(g4) = -14.35
FEATURE [PartDesign::Pad] Pad009
  BaseFeature = -> Pad007
  Direction = (1,1,1)
  Length = 1
  Length2 = 100
  Placement = pos=(0.2,0,0) rot=(0.57735,0.57735,0.57735;2.0944rad)
  Profile = -> Sketch009
  Refine = true
  Reversed = true
  Type = 0
FEATURE [PartDesign::Body] Body004  label="Display Frame Bottom"
  Group = -> [Sketch007,Pad007,Pad009,Sketch009]
  Origin = -> Origin005
  Tip = -> Pad009
FEATURE [Sketcher::SketchObject] Sketch010  label="Sketch011"
  FullyConstrained = true
  MapMode = 5
  Placement = pos=(0.2,0,0) rot=(0.57735,0.57735,0.57735;2.0944rad)
  Support = -> [DatumPlane001]
  expr: Constraints[9] = Sketch007.Constraints[16]
  expr: Constraints[10] = Sketch006.Constraints[21]
  expr: Constraints[11] = Sketch006.Constraints[19]
  sketch-geometry (4):
    g0: LineSegment StartX=0 StartY=9.55 StartZ=0 EndX=3.3 EndY=9.55 EndZ=0
    g1: LineSegment StartX=3.3 StartY=9.55 StartZ=0 EndX=3.3 EndY=-2.95 EndZ=0
    g2: LineSegment StartX=3.3 StartY=-2.95 StartZ=0 EndX=0 EndY=-2.95 EndZ=0
    g3: LineSegment StartX=0 StartY=-2.95 StartZ=0 EndX=0 EndY=9.55 EndZ=0
  constraints (12):
    c: Coincident(g0,g1)
    c: Coincident(g1,g2)
    c: Coincident(g2,g3)
    c: Coincident(g3,g0)
    c: Horizontal(g0)
    c: Horizontal(g2)
    c: Vertical(g1)
    c: Vertical(g3)
    c: PointOnObject(g0,g-2)
    c: DistanceY(g1) = -2.95
    c: DistanceY(g0) = 9.55
    c: DistanceX(g0) = 3.3
FEATURE [Sketcher::SketchObject] Sketch011  label="Sketch012"
  FullyConstrained = true
  MapMode = 5
  Placement = pos=(0,0,0) rot=(1,0,0;1.5708rad)
  Support = -> [XZ_Plane]
  sketch-geometry (5):
    g0: LineSegment StartX=-18.5 StartY=13.7 StartZ=0 EndX=-15.5 EndY=13.7 EndZ=0
    g1: LineSegment StartX=-15.5 StartY=13.7 StartZ=0 EndX=-15.5 EndY=-13.7 EndZ=0
    g2: LineSegment StartX=-15.5 StartY=-13.7 StartZ=0 EndX=-18.5 EndY=-13.7 EndZ=0
    g3: LineSegment StartX=-18.5 StartY=-13.7 StartZ=0 EndX=-18.5 EndY=13.7 EndZ=0
    g4: GeomPoint X=-17 Y=0 Z=0
  constraints (13):
    c: Coincident(g0,g1)
    c: Coincident(g1,g2)
    c: Coincident(g2,g3)
    c: Coincident(g3,g0)
    c: Horizontal(g0)
    c: Horizontal(g2)
    c: Vertical(g1)
    c: Vertical(g3)
    c: PointOnObject(g4,g-1)
    c: Symmetric(g0,g1,g4)
    c: Distance(g3) = 27.4
    c: Distance(g2) = 3
    c: DistanceX(g4) = -17
FEATURE [Sketcher::SketchObject] Sketch012  label="Case Outline"
  FullyConstrained = true
  MapMode = 5
  Placement = pos=(0,0,0) rot=(1,0,0;1.5708rad)
  Support = -> [XZ_Plane002]
  sketch-geometry (4):
    g0: LineSegment StartX=-52.5 StartY=-14.35 StartZ=0 EndX=52.5 EndY=-14.35 EndZ=0
    g1: LineSegment StartX=52.5 StartY=-14.35 StartZ=0 EndX=52.5 EndY=14.35 EndZ=0
    g2: LineSegment StartX=52.5 StartY=14.35 StartZ=0 EndX=-52.5 EndY=14.35 EndZ=0
    g3: LineSegment StartX=-52.5 StartY=14.35 StartZ=0 EndX=-52.5 EndY=-14.35 EndZ=0
  constraints (10):
    c: Coincident(g0,g1)
    c: Coincident(g1,g2)
    c: Coincident(g2,g3)
    c: Coincident(g3,g0)
    c: Horizontal(g0)
    c: Vertical(g1)
    c: Symmetric(g2,g0,g-1)
    c: Symmetric(g2,g1,g-2)
    c: Distance(g2) = 105
    c: Distance(g3) = 28.7
FEATURE [Sketcher::SketchObject] Sketch013
  FullyConstrained = true
  MapMode = 5
  Placement = pos=(0,0,0) rot=(1,0,0;1.5708rad)
  Support = -> [XZ_Plane001]
  expr: Constraints[8] = Sketch012.Constraints[8]
  expr: Constraints[9] = Sketch012.Constraints[9]
  sketch-geometry (4):
    g0: LineSegment StartX=-52.5 StartY=-14.35 StartZ=0 EndX=52.5 EndY=-14.35 EndZ=0
    g1: LineSegment StartX=52.5 StartY=-14.35 StartZ=0 EndX=52.5 EndY=14.35 EndZ=0
    g2: LineSegment StartX=52.5 StartY=14.35 StartZ=0 EndX=-52.5 EndY=14.35 EndZ=0
    g3: LineSegment StartX=-52.5 StartY=14.35 StartZ=0 EndX=-52.5 EndY=-14.35 EndZ=0
  constraints (10):
    c: Coincident(g0,g1)
    c: Coincident(g1,g2)
    c: Coincident(g2,g3)
    c: Coincident(g3,g0)
    c: Horizontal(g0)
    c: Vertical(g1)
    c: Symmetric(g2,g0,g-1)
    c: Symmetric(g2,g1,g-2)
    c: Distance(g2) = 105
    c: Distance(g3) = 28.7
FEATURE [PartDesign::Pad] Pad001
  Direction = (1,1,1)
  Length = 5
  Length2 = 100
  Placement = pos=(0,0,0) rot=(1,0,0;1.5708rad)
  Profile = -> Sketch013
  Refine = true
  Reversed = true
  Type = 0
FEATURE [PartDesign::Pad] Pad002
  BaseFeature = -> Pad001
  Direction = (1,1,1)
  Length = 2.5
  Length2 = 100
  Placement = pos=(0,0,0) rot=(1,0,0;1.5708rad)
  Profile = -> Sketch013
  Refine = true
  Type = 0
FEATURE [PartDesign::Fillet] Fillet001
  Base = -> Pad002 [Edge5,Edge12,Edge11,Edge7]
  BaseFeature = -> Pad002
  Placement = pos=(0,0,0) rot=(1,0,0;1.5708rad)
  Radius = 2.5
  Refine = true
  SupportTransform = false
FEATURE [PartDesign::Thickness] Thickness001
  Base = -> Fillet001 [Face10,Face1]
  BaseFeature = -> Fillet001
  Intersection = false
  Join = 0
  Mode = 0
  Refine = true
  SupportTransform = false
  Value = 2
FEATURE [PartDesign::Pocket] Pocket
  BaseFeature = -> Thickness001
  Length = 5
  Length2 = 100
  Profile = -> Sketch
  Refine = true
  Type = 1
FEATURE [PartDesign::MultiTransform] MultiTransform
  BaseFeature = -> Pocket
  Originals = -> [Pocket]
  Refine = true
  Transformations = -> [LinearPattern,Mirrored]
FEATURE [PartDesign::Pocket] Pocket001
  BaseFeature = -> MultiTransform
  Length = 5
  Length2 = 100
  Profile = -> Sketch001
  Refine = true
  Type = 1
FEATURE [PartDesign::MultiTransform] MultiTransform001
  BaseFeature = -> Pocket001
  Originals = -> [Pocket001]
  Refine = true
  Transformations = -> [LinearPattern001,Mirrored001]
FEATURE [PartDesign::Body] Body001  label="Outer Frame"
  Group = -> [Pad001,Pad002,Fillet001,Thickness001,DatumPlane,Sketch,Pocket,MultiTransform,LinearPattern,Mirrored,Sketch001,Pocket001,MultiTransform001,LinearPattern001,Mirrored001,Sketch013]
  Origin = -> Origin001
  Tip = -> MultiTransform001
FEATURE [Sketcher::SketchObject] Sketch014
  FullyConstrained = true
  MapMode = 5
  Placement = pos=(0,0,0) rot=(1,0,0;1.5708rad)
  Support = -> [XZ_Plane]
  expr: Constraints[8] = Sketch012.Constraints[8]
  expr: Constraints[9] = Sketch012.Constraints[9]
  sketch-geometry (4):
    g0: LineSegment StartX=-52.5 StartY=-14.35 StartZ=0 EndX=52.5 EndY=-14.35 EndZ=0
    g1: LineSegment StartX=52.5 StartY=-14.35 StartZ=0 EndX=52.5 EndY=14.35 EndZ=0
    g2: LineSegment StartX=52.5 StartY=14.35 StartZ=0 EndX=-52.5 EndY=14.35 EndZ=0
    g3: LineSegment StartX=-52.5 StartY=14.35 StartZ=0 EndX=-52.5 EndY=-14.35 EndZ=0
  constraints (10):
    c: Coincident(g0,g1)
    c: Coincident(g1,g2)
    c: Coincident(g2,g3)
    c: Coincident(g3,g0)
    c: Horizontal(g0)
    c: Vertical(g1)
    c: Symmetric(g2,g0,g-1)
    c: Symmetric(g2,g1,g-2)
    c: Distance(g2) = 105
    c: Distance(g3) = 28.7
FEATURE [PartDesign::Pad] Pad
  Direction = (1,1,1)
  Length = 1
  Length2 = 100
  Placement = pos=(0,0,0) rot=(1,0,0;1.5708rad)
  Profile = -> Sketch014
  Refine = true
  Reversed = true
  Type = 0
FEATURE [PartDesign::Thickness] Thickness
  Base = -> Pad [Face5,Face6]
  BaseFeature = -> Pad
  Intersection = false
  Join = 0
  Mode = 0
  Refine = true
  Reversed = true
  SupportTransform = false
  Value = 3
FEATURE [PartDesign::Fillet] Fillet
  Base = -> Thickness [Edge17,Edge19,Edge23,Edge24]
  BaseFeature = -> Thickness
  Radius = 0.5
  Refine = true
  SupportTransform = false
FEATURE [PartDesign::Fillet] Fillet003
  Base = -> Fillet [Edge32,Edge29,Edge34,Edge30]
  BaseFeature = -> Fillet
  Radius = 2.5
  Refine = true
  SupportTransform = false
FEATURE [PartDesign::Boolean] Boolean
  BaseFeature = -> Fillet003
  Group = -> [Body003,Body004]
  Refine = true
  Type = 0
FEATURE [PartDesign::Pad] Pad010
  BaseFeature = -> Boolean
  Direction = (1,1,1)
  Length = 1
  Length2 = 100
  Profile = -> Sketch010
  Refine = true
  Reversed = true
  Type = 0
FEATURE [PartDesign::Pad] Pad011
  BaseFeature = -> Pad010
  Direction = (1,1,1)
  Length = 1
  Length2 = 100
  Profile = -> Sketch011
  Refine = true
  Reversed = true
  Type = 0
  expr: Length = Pad.Length
FEATURE [PartDesign::Chamfer] Chamfer001
  Angle = 45
  Base = -> Pad011 [Edge81,Edge80,Edge106,Edge104,Edge105]
  BaseFeature = -> Pad011
  ChamferType = 0
  FlipDirection = false
  Refine = true
  Size = 0.4
  Size2 = 1
  SupportTransform = false
FEATURE [PartDesign::Hole] Hole
  BaseFeature = -> Pad005
  Depth = 25
  DepthType = 1
  Diameter = 2
  DrillForDepth = false
  DrillPoint = 1
  DrillPointAngle = 118
  HoleCutCountersinkAngle = 90
  HoleCutCustomValues = false
  HoleCutDepth = 0
  HoleCutDiameter = 6.1
  HoleCutType = 0
  ModelActualThread = false
  Placement = pos=(0,0,0) rot=(1,0,0;1.5708rad)
  Profile = -> Sketch004
  Refine = true
  Tapered = false
  TaperedAngle = 90
  ThreadAngle = 0
  ThreadClass = 0
  ThreadCutOffInner = 0
  ThreadCutOffOuter = 0
  ThreadDirection = 0
  ThreadFit = 0
  ThreadPitch = 0
  ThreadSize = 0
  ThreadType = 0
  Threaded = false
FEATURE [PartDesign::Body] Body002  label="Button"
  Group = -> [Sketch004,Sketch005,Pad004,Pad005,Hole]
  Origin = -> Origin003
  Tip = -> Hole
FEATURE [Sketcher::SketchObject] Sketch015
  FullyConstrained = true
  MapMode = 5
  Placement = pos=(0,0,0) rot=(1,0,0;1.5708rad)
  Support = -> [XZ_Plane]
  sketch-geometry (5):
    g0: LineSegment StartX=-38 StartY=14.35 StartZ=0 EndX=-34 EndY=14.35 EndZ=0
    g1: LineSegment StartX=-34 StartY=14.35 StartZ=0 EndX=-34 EndY=-14.35 EndZ=0
    g2: LineSegment StartX=-34 StartY=-14.35 StartZ=0 EndX=-38 EndY=-14.35 EndZ=0
    g3: LineSegment StartX=-38 StartY=-14.35 StartZ=0 EndX=-38 EndY=14.35 EndZ=0
    g4: GeomPoint X=-36 Y=0 Z=0
  constraints (13):
    c: Coincident(g0,g1)
    c: Coincident(g1,g2)
    c: Coincident(g2,g3)
    c: Coincident(g3,g0)
    c: Horizontal(g0)
    c: Horizontal(g2)
    c: Vertical(g1)
    c: Vertical(g3)
    c: PointOnObject(g4,g-1)
    c: Symmetric(g0,g1,g4)
    c: DistanceX(g4) = -36
    c: Distance(g2) = 4
    c: Distance(g3) = 28.7
FEATURE [PartDesign::Pad] Pad012
  BaseFeature = -> Chamfer001
  Direction = (1,1,1)
  Length = 1
  Length2 = 100
  Profile = -> Sketch015
  Refine = true
  Reversed = true
  Type = 0
FEATURE [Sketcher::SketchObject] Sketch016
  FullyConstrained = true
  MapMode = 5
  Placement = pos=(0,0,0) rot=(1,0,0;1.5708rad)
  Support = -> [XZ_Plane]
  sketch-geometry (1):
    g0: Circle CenterX=46.5 CenterY=10.85 CenterZ=0 NormalX=0 NormalY=0 NormalZ=1 AngleXU=0 Radius=3.5
  constraints (3):
    c: Radius(g0) = 3.5
    c: DistanceX(g0) = 46.5
    c: DistanceY(g0) = 10.85
FEATURE [PartDesign::Pad] Pad013
  BaseFeature = -> Pad012
  Direction = (1,1,1)
  Length = 1
  Length2 = 100
  Profile = -> Sketch016
  Refine = true
  Reversed = true
  Type = 0
FEATURE [PartDesign::LinearPattern] LinearPattern002
  Direction = -> Z_Axis
  Length = 21.7
  Occurrences = 2
  Refine = true
  Reversed = true
FEATURE [PartDesign::LinearPattern] LinearPattern003
  Direction = -> X_Axis
  Length = 93
  Occurrences = 2
  Refine = true
  Reversed = true
FEATURE [PartDesign::Hole] Hole001
  BaseFeature = -> Pad013
  Depth = 25
  DepthType = 1
  Diameter = 3.3
  DrillForDepth = false
  DrillPoint = 1
  DrillPointAngle = 118
  HoleCutCountersinkAngle = 90
  HoleCutCustomValues = false
  HoleCutDepth = 0
  HoleCutDiameter = 6.1
  HoleCutType = 0
  ModelActualThread = false
  Profile = -> Sketch016
  Refine = true
  Tapered = false
  TaperedAngle = 90
  ThreadAngle = 0
  ThreadClass = 0
  ThreadCutOffInner = 0
  ThreadCutOffOuter = 0
  ThreadDirection = 0
  ThreadFit = 0
  ThreadPitch = 0
  ThreadSize = 0
  ThreadType = 0
  Threaded = false
FEATURE [PartDesign::MultiTransform] MultiTransform002
  BaseFeature = -> Hole001
  Originals = -> [Pad013,Hole001]
  Refine = true
  Transformations = -> [LinearPattern002,LinearPattern003]
FEATURE [PartDesign::Fillet] Fillet004
  Base = -> MultiTransform002 [Edge148,Edge157,Edge160,Edge151,Edge149,Edge146,Edge140,Edge142,Edge143,Edge138,Edge70,Edge81,Edge61,Edge63,Edge87,Edge91,Edge89,Edge122,Edge121,Edge92]
  BaseFeature = -> MultiTransform002
  Radius = 1
  Refine = true
  SupportTransform = false
FEATURE [PartDesign::Fillet] Fillet005
  Base = -> Fillet004 [Edge100,Edge113,Edge110]
  BaseFeature = -> Fillet004
  Radius = 0.2
  Refine = true
  SupportTransform = false
FEATURE [PartDesign::Body] Body  label="Inner Frame"
  Group = -> [Pad,Thickness,Fillet,Fillet003,Boolean,Sketch010,Pad010,Sketch011,Pad011,Chamfer001,Sketch014,Sketch015,Pad012,Sketch016,Pad013,Hole001,MultiTransform002,LinearPattern002,LinearPattern003,Fillet004,Fillet005]
  Origin = -> Origin
  Tip = -> Fillet005
FEATURE [App::Part] Bezel
  Group = -> [LCS_0,Body001,Body,Sketch012,Body002]
  Origin = -> Origin002
